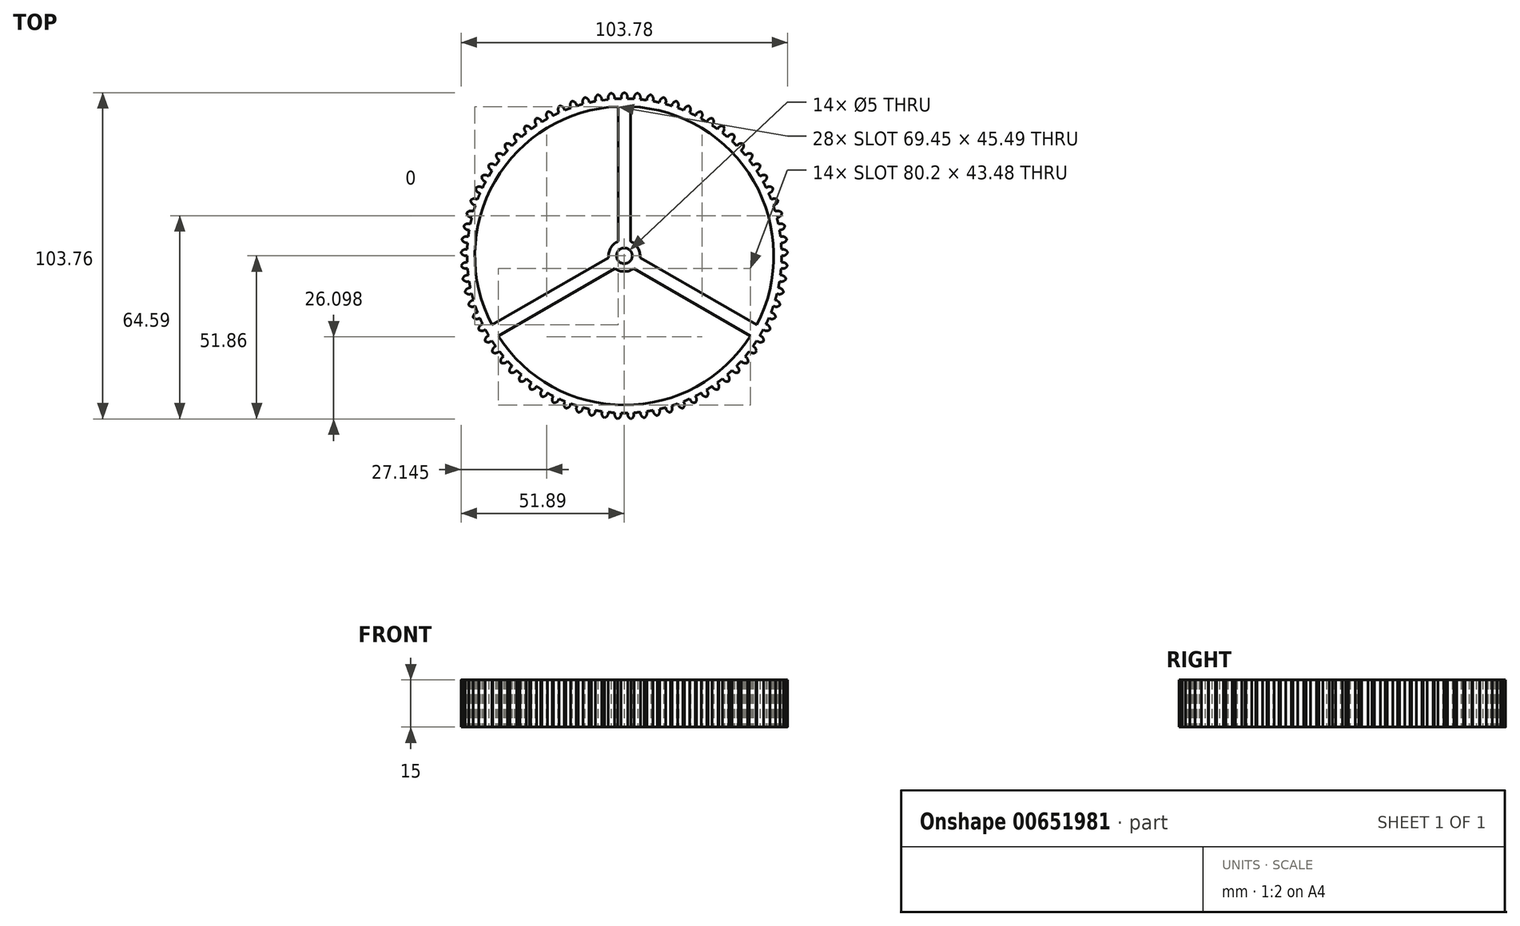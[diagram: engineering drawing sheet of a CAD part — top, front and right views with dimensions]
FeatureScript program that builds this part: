
annotation { "Feature Type Name" : "Feature", "Feature Type Description" : "" }
export const myFeature = defineFeature(function(context is Context, id is Id, definition is map)
    precondition{}
    {
        {
            var Q0;
            Q0=qCreatedBy(makeId("Top.planeOp"),FACE);
            var sketch = newSketch(context, id + "F0", { "sketchPlane" : qUnion([Q0])});
            skArc(sketch, "E0", {"start": v(-1, 49.99) * mm, "mid": v(-2.04, 49.96) * mm, "end": v(-3.08, 49.9) * mm});
            skLineSegment(sketch, "E1", {"start": v(-1, 49.99) * mm, "end": v(-1, 51.99) * mm});
            skLineSegment(sketch, "E2", {"start": v(-1, 51.99) * mm, "end": v(1, 51.99) * mm});
            skLineSegment(sketch, "E3", {"start": v(1, 51.99) * mm, "end": v(1, 49.99) * mm});
            skLineSegment(sketch, "E4.1.0", {"start": v(-5.23, 51.74) * mm, "end": v(-3.24, 51.9) * mm});
            skLineSegment(sketch, "E4.1.1", {"start": v(-3.24, 51.9) * mm, "end": v(-3.08, 49.9) * mm});
            skLineSegment(sketch, "E4.1.2", {"start": v(-5.07, 49.74) * mm, "end": v(-5.23, 51.74) * mm});
            skLineSegment(sketch, "E4.2.0", {"start": v(-9.43, 51.14) * mm, "end": v(-7.46, 51.46) * mm});
            skLineSegment(sketch, "E4.2.1", {"start": v(-7.46, 51.46) * mm, "end": v(-7.14, 49.49) * mm});
            skLineSegment(sketch, "E4.2.2", {"start": v(-9.1, 49.16) * mm, "end": v(-9.43, 51.14) * mm});
            skLineSegment(sketch, "E4.3.0", {"start": v(-13.57, 50.2) * mm, "end": v(-11.63, 50.68) * mm});
            skLineSegment(sketch, "E4.3.1", {"start": v(-11.63, 50.68) * mm, "end": v(-11.14, 48.74) * mm});
            skLineSegment(sketch, "E4.3.2", {"start": v(-13.09, 48.26) * mm, "end": v(-13.57, 50.2) * mm});
            skLineSegment(sketch, "E4.4.0", {"start": v(-17.62, 48.92) * mm, "end": v(-15.72, 49.57) * mm});
            skLineSegment(sketch, "E4.4.1", {"start": v(-15.72, 49.57) * mm, "end": v(-15.08, 47.67) * mm});
            skLineSegment(sketch, "E4.4.2", {"start": v(-16.98, 47.03) * mm, "end": v(-17.62, 48.92) * mm});
            skLineSegment(sketch, "E4.5.0", {"start": v(-21.55, 47.33) * mm, "end": v(-19.7, 48.12) * mm});
            skLineSegment(sketch, "E4.5.1", {"start": v(-19.7, 48.12) * mm, "end": v(-18.92, 46.28) * mm});
            skLineSegment(sketch, "E4.5.2", {"start": v(-20.75, 45.5) * mm, "end": v(-21.55, 47.33) * mm});
            skLineSegment(sketch, "E4.6.0", {"start": v(-25.33, 45.41) * mm, "end": v(-23.57, 46.35) * mm});
            skLineSegment(sketch, "E4.6.1", {"start": v(-23.57, 46.35) * mm, "end": v(-22.63, 44.59) * mm});
            skLineSegment(sketch, "E4.6.2", {"start": v(-24.4, 43.65) * mm, "end": v(-25.33, 45.41) * mm});
            skLineSegment(sketch, "E4.7.0", {"start": v(-28.95, 43.2) * mm, "end": v(-27.27, 44.28) * mm});
            skLineSegment(sketch, "E4.7.1", {"start": v(-27.27, 44.28) * mm, "end": v(-26.18, 42.6) * mm});
            skLineSegment(sketch, "E4.7.2", {"start": v(-27.87, 41.51) * mm, "end": v(-28.95, 43.2) * mm});
            skLineSegment(sketch, "E4.8.0", {"start": v(-32.37, 40.7) * mm, "end": v(-30.78, 41.9) * mm});
            skLineSegment(sketch, "E4.8.1", {"start": v(-30.78, 41.9) * mm, "end": v(-29.57, 40.32) * mm});
            skLineSegment(sketch, "E4.8.2", {"start": v(-31.16, 39.1) * mm, "end": v(-32.37, 40.7) * mm});
            skLineSegment(sketch, "E4.9.0", {"start": v(-35.58, 37.92) * mm, "end": v(-34.1, 39.26) * mm});
            skLineSegment(sketch, "E4.9.1", {"start": v(-34.1, 39.26) * mm, "end": v(-32.76, 37.78) * mm});
            skLineSegment(sketch, "E4.9.2", {"start": v(-34.24, 36.43) * mm, "end": v(-35.58, 37.92) * mm});
            skLineSegment(sketch, "E4.10.0", {"start": v(-38.55, 34.9) * mm, "end": v(-37.18, 36.35) * mm});
            skLineSegment(sketch, "E4.10.1", {"start": v(-37.18, 36.35) * mm, "end": v(-35.73, 34.98) * mm});
            skLineSegment(sketch, "E4.10.2", {"start": v(-37.1, 33.52) * mm, "end": v(-38.55, 34.9) * mm});
            skLineSegment(sketch, "E4.11.0", {"start": v(-41.27, 31.63) * mm, "end": v(-40.02, 33.2) * mm});
            skLineSegment(sketch, "E4.11.1", {"start": v(-40.02, 33.2) * mm, "end": v(-38.46, 31.95) * mm});
            skLineSegment(sketch, "E4.11.2", {"start": v(-39.7, 30.39) * mm, "end": v(-41.27, 31.63) * mm});
            skLineSegment(sketch, "E4.12.0", {"start": v(-43.71, 28.17) * mm, "end": v(-42.6, 29.83) * mm});
            skLineSegment(sketch, "E4.12.1", {"start": v(-42.6, 29.83) * mm, "end": v(-40.93, 28.7) * mm});
            skLineSegment(sketch, "E4.12.2", {"start": v(-42.05, 27.05) * mm, "end": v(-43.71, 28.17) * mm});
            skLineSegment(sketch, "E4.13.0", {"start": v(-45.86, 24.5) * mm, "end": v(-44.88, 26.25) * mm});
            skLineSegment(sketch, "E4.13.1", {"start": v(-44.88, 26.25) * mm, "end": v(-43.14, 25.28) * mm});
            skLineSegment(sketch, "E4.13.2", {"start": v(-44.11, 23.53) * mm, "end": v(-45.86, 24.5) * mm});
            skLineSegment(sketch, "E4.14.0", {"start": v(-47.7, 20.69) * mm, "end": v(-46.87, 22.5) * mm});
            skLineSegment(sketch, "E4.14.1", {"start": v(-46.87, 22.5) * mm, "end": v(-45.06, 21.68) * mm});
            skLineSegment(sketch, "E4.14.2", {"start": v(-45.89, 19.86) * mm, "end": v(-47.7, 20.69) * mm});
            skLineSegment(sketch, "E4.15.0", {"start": v(-49.23, 16.73) * mm, "end": v(-48.55, 18.61) * mm});
            skLineSegment(sketch, "E4.15.1", {"start": v(-48.55, 18.61) * mm, "end": v(-46.67, 17.93) * mm});
            skLineSegment(sketch, "E4.15.2", {"start": v(-47.35, 16.05) * mm, "end": v(-49.23, 16.73) * mm});
            skLineSegment(sketch, "E4.16.0", {"start": v(-50.43, 12.66) * mm, "end": v(-49.9, 14.6) * mm});
            skLineSegment(sketch, "E4.16.1", {"start": v(-49.9, 14.6) * mm, "end": v(-47.98, 14.07) * mm});
            skLineSegment(sketch, "E4.16.2", {"start": v(-48.5, 12.14) * mm, "end": v(-50.43, 12.66) * mm});
            skLineSegment(sketch, "E4.17.0", {"start": v(-51.3, 8.51) * mm, "end": v(-50.93, 10.48) * mm});
            skLineSegment(sketch, "E4.17.1", {"start": v(-50.93, 10.48) * mm, "end": v(-48.97, 10.11) * mm});
            skLineSegment(sketch, "E4.17.2", {"start": v(-49.33, 8.15) * mm, "end": v(-51.3, 8.51) * mm});
            skLineSegment(sketch, "E4.18.0", {"start": v(-51.82, 4.3) * mm, "end": v(-51.62, 6.3) * mm});
            skLineSegment(sketch, "E4.18.1", {"start": v(-51.62, 6.3) * mm, "end": v(-49.63, 6.09) * mm});
            skLineSegment(sketch, "E4.18.2", {"start": v(-49.83, 4.1) * mm, "end": v(-51.82, 4.3) * mm});
            skLineSegment(sketch, "E4.19.0", {"start": v(-52, 0.06) * mm, "end": v(-51.96, 2.06) * mm});
            skLineSegment(sketch, "E4.19.1", {"start": v(-51.96, 2.06) * mm, "end": v(-49.96, 2.02) * mm});
            skLineSegment(sketch, "E4.19.2", {"start": v(-50, 0.02) * mm, "end": v(-52, 0.06) * mm});
            skLineSegment(sketch, "E4.20.0", {"start": v(-51.83, -4.18) * mm, "end": v(-51.95, -2.18) * mm});
            skLineSegment(sketch, "E4.20.1", {"start": v(-51.95, -2.18) * mm, "end": v(-49.96, -2.06) * mm});
            skLineSegment(sketch, "E4.20.2", {"start": v(-49.83, -4.05) * mm, "end": v(-51.83, -4.18) * mm});
            skLineSegment(sketch, "E4.21.0", {"start": v(-51.32, -8.39) * mm, "end": v(-51.6, -6.4) * mm});
            skLineSegment(sketch, "E4.21.1", {"start": v(-51.6, -6.4) * mm, "end": v(-49.62, -6.12) * mm});
            skLineSegment(sketch, "E4.21.2", {"start": v(-49.34, -8.1) * mm, "end": v(-51.32, -8.39) * mm});
            skLineSegment(sketch, "E4.22.0", {"start": v(-50.46, -12.54) * mm, "end": v(-50.9, -10.6) * mm});
            skLineSegment(sketch, "E4.22.1", {"start": v(-50.9, -10.6) * mm, "end": v(-48.96, -10.15) * mm});
            skLineSegment(sketch, "E4.22.2", {"start": v(-48.51, -12.1) * mm, "end": v(-50.46, -12.54) * mm});
            skLineSegment(sketch, "E4.23.0", {"start": v(-49.27, -16.61) * mm, "end": v(-49.87, -14.7) * mm});
            skLineSegment(sketch, "E4.23.1", {"start": v(-49.87, -14.7) * mm, "end": v(-47.97, -14.1) * mm});
            skLineSegment(sketch, "E4.23.2", {"start": v(-47.36, -16.01) * mm, "end": v(-49.27, -16.61) * mm});
            skLineSegment(sketch, "E4.24.0", {"start": v(-47.75, -20.57) * mm, "end": v(-48.5, -18.72) * mm});
            skLineSegment(sketch, "E4.24.1", {"start": v(-48.5, -18.72) * mm, "end": v(-46.66, -17.97) * mm});
            skLineSegment(sketch, "E4.24.2", {"start": v(-45.9, -19.82) * mm, "end": v(-47.75, -20.57) * mm});
            skLineSegment(sketch, "E4.25.0", {"start": v(-45.92, -24.4) * mm, "end": v(-46.82, -22.61) * mm});
            skLineSegment(sketch, "E4.25.1", {"start": v(-46.82, -22.61) * mm, "end": v(-45.04, -21.7) * mm});
            skLineSegment(sketch, "E4.25.2", {"start": v(-44.13, -23.5) * mm, "end": v(-45.92, -24.4) * mm});
            skLineSegment(sketch, "E4.26.0", {"start": v(-43.78, -28.06) * mm, "end": v(-44.82, -26.35) * mm});
            skLineSegment(sketch, "E4.26.1", {"start": v(-44.82, -26.35) * mm, "end": v(-43.12, -25.3) * mm});
            skLineSegment(sketch, "E4.26.2", {"start": v(-42.07, -27.01) * mm, "end": v(-43.78, -28.06) * mm});
            skLineSegment(sketch, "E4.27.0", {"start": v(-41.34, -31.53) * mm, "end": v(-42.53, -29.92) * mm});
            skLineSegment(sketch, "E4.27.1", {"start": v(-42.53, -29.92) * mm, "end": v(-40.91, -28.74) * mm});
            skLineSegment(sketch, "E4.27.2", {"start": v(-39.73, -30.35) * mm, "end": v(-41.34, -31.53) * mm});
            skLineSegment(sketch, "E4.28.0", {"start": v(-38.64, -34.8) * mm, "end": v(-39.94, -33.29) * mm});
            skLineSegment(sketch, "E4.28.1", {"start": v(-39.94, -33.29) * mm, "end": v(-38.43, -31.98) * mm});
            skLineSegment(sketch, "E4.28.2", {"start": v(-37.12, -33.49) * mm, "end": v(-38.64, -34.8) * mm});
            skLineSegment(sketch, "E4.29.0", {"start": v(-35.67, -37.83) * mm, "end": v(-37.1, -36.43) * mm});
            skLineSegment(sketch, "E4.29.1", {"start": v(-37.1, -36.43) * mm, "end": v(-35.7, -35) * mm});
            skLineSegment(sketch, "E4.29.2", {"start": v(-34.27, -36.4) * mm, "end": v(-35.67, -37.83) * mm});
            skLineSegment(sketch, "E4.30.0", {"start": v(-32.47, -40.61) * mm, "end": v(-34, -39.33) * mm});
            skLineSegment(sketch, "E4.30.1", {"start": v(-34, -39.33) * mm, "end": v(-32.73, -37.8) * mm});
            skLineSegment(sketch, "E4.30.2", {"start": v(-31.19, -39.08) * mm, "end": v(-32.47, -40.61) * mm});
            skLineSegment(sketch, "E4.31.0", {"start": v(-29.05, -43.12) * mm, "end": v(-30.69, -41.98) * mm});
            skLineSegment(sketch, "E4.31.1", {"start": v(-30.69, -41.98) * mm, "end": v(-29.54, -40.34) * mm});
            skLineSegment(sketch, "E4.31.2", {"start": v(-27.9, -41.49) * mm, "end": v(-29.05, -43.12) * mm});
            skLineSegment(sketch, "E4.32.0", {"start": v(-25.44, -45.35) * mm, "end": v(-27.16, -44.34) * mm});
            skLineSegment(sketch, "E4.32.1", {"start": v(-27.16, -44.34) * mm, "end": v(-26.15, -42.61) * mm});
            skLineSegment(sketch, "E4.32.2", {"start": v(-24.43, -43.62) * mm, "end": v(-25.44, -45.35) * mm});
            skLineSegment(sketch, "E4.33.0", {"start": v(-21.66, -47.27) * mm, "end": v(-23.46, -46.4) * mm});
            skLineSegment(sketch, "E4.33.1", {"start": v(-23.46, -46.4) * mm, "end": v(-22.6, -44.6) * mm});
            skLineSegment(sketch, "E4.33.2", {"start": v(-20.79, -45.47) * mm, "end": v(-21.66, -47.27) * mm});
            skLineSegment(sketch, "E4.34.0", {"start": v(-17.73, -48.88) * mm, "end": v(-19.6, -48.16) * mm});
            skLineSegment(sketch, "E4.34.1", {"start": v(-19.6, -48.16) * mm, "end": v(-18.88, -46.3) * mm});
            skLineSegment(sketch, "E4.34.2", {"start": v(-17.01, -47.01) * mm, "end": v(-17.73, -48.88) * mm});
            skLineSegment(sketch, "E4.35.0", {"start": v(-13.69, -50.16) * mm, "end": v(-15.6, -49.6) * mm});
            skLineSegment(sketch, "E4.35.1", {"start": v(-15.6, -49.6) * mm, "end": v(-15.04, -47.68) * mm});
            skLineSegment(sketch, "E4.35.2", {"start": v(-13.12, -48.24) * mm, "end": v(-13.69, -50.16) * mm});
            skLineSegment(sketch, "E4.36.0", {"start": v(-9.55, -51.11) * mm, "end": v(-11.51, -50.7) * mm});
            skLineSegment(sketch, "E4.36.1", {"start": v(-11.51, -50.7) * mm, "end": v(-11.1, -48.75) * mm});
            skLineSegment(sketch, "E4.36.2", {"start": v(-9.15, -49.15) * mm, "end": v(-9.55, -51.11) * mm});
            skLineSegment(sketch, "E4.37.0", {"start": v(-5.36, -51.72) * mm, "end": v(-7.34, -51.47) * mm});
            skLineSegment(sketch, "E4.37.1", {"start": v(-7.34, -51.47) * mm, "end": v(-7.1, -49.49) * mm});
            skLineSegment(sketch, "E4.37.2", {"start": v(-5.11, -49.73) * mm, "end": v(-5.36, -51.72) * mm});
            skLineSegment(sketch, "E4.38.0", {"start": v(-1.12, -51.98) * mm, "end": v(-3.12, -51.9) * mm});
            skLineSegment(sketch, "E4.38.1", {"start": v(-3.12, -51.9) * mm, "end": v(-3.04, -49.9) * mm});
            skLineSegment(sketch, "E4.38.2", {"start": v(-1.04, -49.98) * mm, "end": v(-1.12, -51.98) * mm});
            skLineSegment(sketch, "E4.39.0", {"start": v(3.12, -51.9) * mm, "end": v(1.12, -51.98) * mm});
            skLineSegment(sketch, "E4.39.1", {"start": v(1.12, -51.98) * mm, "end": v(1.04, -49.98) * mm});
            skLineSegment(sketch, "E4.39.2", {"start": v(3.04, -49.9) * mm, "end": v(3.12, -51.9) * mm});
            skLineSegment(sketch, "E4.40.0", {"start": v(7.34, -51.47) * mm, "end": v(5.35, -51.72) * mm});
            skLineSegment(sketch, "E4.40.1", {"start": v(5.35, -51.72) * mm, "end": v(5.11, -49.73) * mm});
            skLineSegment(sketch, "E4.40.2", {"start": v(7.1, -49.49) * mm, "end": v(7.34, -51.47) * mm});
            skLineSegment(sketch, "E4.41.0", {"start": v(11.51, -50.7) * mm, "end": v(9.55, -51.11) * mm});
            skLineSegment(sketch, "E4.41.1", {"start": v(9.55, -51.11) * mm, "end": v(9.15, -49.15) * mm});
            skLineSegment(sketch, "E4.41.2", {"start": v(11.1, -48.75) * mm, "end": v(11.51, -50.7) * mm});
            skLineSegment(sketch, "E4.42.0", {"start": v(15.6, -49.6) * mm, "end": v(13.69, -50.16) * mm});
            skLineSegment(sketch, "E4.42.1", {"start": v(13.69, -50.16) * mm, "end": v(13.12, -48.24) * mm});
            skLineSegment(sketch, "E4.42.2", {"start": v(15.04, -47.68) * mm, "end": v(15.6, -49.6) * mm});
            skLineSegment(sketch, "E4.43.0", {"start": v(19.6, -48.16) * mm, "end": v(17.73, -48.88) * mm});
            skLineSegment(sketch, "E4.43.1", {"start": v(17.73, -48.88) * mm, "end": v(17.01, -47.01) * mm});
            skLineSegment(sketch, "E4.43.2", {"start": v(18.88, -46.3) * mm, "end": v(19.6, -48.16) * mm});
            skLineSegment(sketch, "E4.44.0", {"start": v(23.46, -46.4) * mm, "end": v(21.66, -47.27) * mm});
            skLineSegment(sketch, "E4.44.1", {"start": v(21.66, -47.27) * mm, "end": v(20.79, -45.47) * mm});
            skLineSegment(sketch, "E4.44.2", {"start": v(22.59, -44.6) * mm, "end": v(23.46, -46.4) * mm});
            skLineSegment(sketch, "E4.45.0", {"start": v(27.16, -44.34) * mm, "end": v(25.44, -45.35) * mm});
            skLineSegment(sketch, "E4.45.1", {"start": v(25.44, -45.35) * mm, "end": v(24.42, -43.62) * mm});
            skLineSegment(sketch, "E4.45.2", {"start": v(26.15, -42.61) * mm, "end": v(27.16, -44.34) * mm});
            skLineSegment(sketch, "E4.46.0", {"start": v(30.69, -41.98) * mm, "end": v(29.05, -43.12) * mm});
            skLineSegment(sketch, "E4.46.1", {"start": v(29.05, -43.12) * mm, "end": v(27.9, -41.49) * mm});
            skLineSegment(sketch, "E4.46.2", {"start": v(29.54, -40.34) * mm, "end": v(30.69, -41.98) * mm});
            skLineSegment(sketch, "E4.47.0", {"start": v(34, -39.33) * mm, "end": v(32.47, -40.61) * mm});
            skLineSegment(sketch, "E4.47.1", {"start": v(32.47, -40.61) * mm, "end": v(31.19, -39.08) * mm});
            skLineSegment(sketch, "E4.47.2", {"start": v(32.73, -37.8) * mm, "end": v(34, -39.33) * mm});
            skLineSegment(sketch, "E4.48.0", {"start": v(37.1, -36.43) * mm, "end": v(35.67, -37.83) * mm});
            skLineSegment(sketch, "E4.48.1", {"start": v(35.67, -37.83) * mm, "end": v(34.27, -36.4) * mm});
            skLineSegment(sketch, "E4.48.2", {"start": v(35.7, -35) * mm, "end": v(37.1, -36.43) * mm});
            skLineSegment(sketch, "E4.49.0", {"start": v(39.94, -33.29) * mm, "end": v(38.63, -34.8) * mm});
            skLineSegment(sketch, "E4.49.1", {"start": v(38.63, -34.8) * mm, "end": v(37.12, -33.49) * mm});
            skLineSegment(sketch, "E4.49.2", {"start": v(38.43, -31.98) * mm, "end": v(39.94, -33.29) * mm});
            skLineSegment(sketch, "E4.50.0", {"start": v(42.52, -29.92) * mm, "end": v(41.34, -31.53) * mm});
            skLineSegment(sketch, "E4.50.1", {"start": v(41.34, -31.53) * mm, "end": v(39.73, -30.35) * mm});
            skLineSegment(sketch, "E4.50.2", {"start": v(40.91, -28.74) * mm, "end": v(42.52, -29.92) * mm});
            skLineSegment(sketch, "E4.51.0", {"start": v(44.82, -26.35) * mm, "end": v(43.78, -28.06) * mm});
            skLineSegment(sketch, "E4.51.1", {"start": v(43.78, -28.06) * mm, "end": v(42.07, -27.01) * mm});
            skLineSegment(sketch, "E4.51.2", {"start": v(43.12, -25.3) * mm, "end": v(44.82, -26.35) * mm});
            skLineSegment(sketch, "E4.52.0", {"start": v(46.82, -22.61) * mm, "end": v(45.92, -24.4) * mm});
            skLineSegment(sketch, "E4.52.1", {"start": v(45.92, -24.4) * mm, "end": v(44.13, -23.5) * mm});
            skLineSegment(sketch, "E4.52.2", {"start": v(45.04, -21.7) * mm, "end": v(46.82, -22.61) * mm});
            skLineSegment(sketch, "E4.53.0", {"start": v(48.5, -18.72) * mm, "end": v(47.75, -20.57) * mm});
            skLineSegment(sketch, "E4.53.1", {"start": v(47.75, -20.57) * mm, "end": v(45.9, -19.82) * mm});
            skLineSegment(sketch, "E4.53.2", {"start": v(46.66, -17.97) * mm, "end": v(48.5, -18.72) * mm});
            skLineSegment(sketch, "E4.54.0", {"start": v(49.87, -14.7) * mm, "end": v(49.27, -16.61) * mm});
            skLineSegment(sketch, "E4.54.1", {"start": v(49.27, -16.61) * mm, "end": v(47.36, -16.01) * mm});
            skLineSegment(sketch, "E4.54.2", {"start": v(47.97, -14.1) * mm, "end": v(49.87, -14.7) * mm});
            skLineSegment(sketch, "E4.55.0", {"start": v(50.9, -10.6) * mm, "end": v(50.46, -12.54) * mm});
            skLineSegment(sketch, "E4.55.1", {"start": v(50.46, -12.54) * mm, "end": v(48.51, -12.1) * mm});
            skLineSegment(sketch, "E4.55.2", {"start": v(48.96, -10.15) * mm, "end": v(50.9, -10.6) * mm});
            skLineSegment(sketch, "E4.56.0", {"start": v(51.6, -6.4) * mm, "end": v(51.32, -8.39) * mm});
            skLineSegment(sketch, "E4.56.1", {"start": v(51.32, -8.39) * mm, "end": v(49.34, -8.1) * mm});
            skLineSegment(sketch, "E4.56.2", {"start": v(49.62, -6.12) * mm, "end": v(51.6, -6.4) * mm});
            skLineSegment(sketch, "E4.57.0", {"start": v(51.95, -2.18) * mm, "end": v(51.83, -4.18) * mm});
            skLineSegment(sketch, "E4.57.1", {"start": v(51.83, -4.18) * mm, "end": v(49.83, -4.05) * mm});
            skLineSegment(sketch, "E4.57.2", {"start": v(49.96, -2.06) * mm, "end": v(51.95, -2.18) * mm});
            skLineSegment(sketch, "E4.58.0", {"start": v(51.96, 2.06) * mm, "end": v(52, 0.06) * mm});
            skLineSegment(sketch, "E4.58.1", {"start": v(52, 0.06) * mm, "end": v(50, 0.02) * mm});
            skLineSegment(sketch, "E4.58.2", {"start": v(49.96, 2.02) * mm, "end": v(51.96, 2.06) * mm});
            skLineSegment(sketch, "E4.59.0", {"start": v(51.62, 6.3) * mm, "end": v(51.82, 4.3) * mm});
            skLineSegment(sketch, "E4.59.1", {"start": v(51.82, 4.3) * mm, "end": v(49.83, 4.1) * mm});
            skLineSegment(sketch, "E4.59.2", {"start": v(49.63, 6.09) * mm, "end": v(51.62, 6.3) * mm});
            skLineSegment(sketch, "E4.60.0", {"start": v(50.93, 10.48) * mm, "end": v(51.3, 8.51) * mm});
            skLineSegment(sketch, "E4.60.1", {"start": v(51.3, 8.51) * mm, "end": v(49.33, 8.15) * mm});
            skLineSegment(sketch, "E4.60.2", {"start": v(48.97, 10.11) * mm, "end": v(50.93, 10.48) * mm});
            skLineSegment(sketch, "E4.61.0", {"start": v(49.9, 14.6) * mm, "end": v(50.43, 12.66) * mm});
            skLineSegment(sketch, "E4.61.1", {"start": v(50.43, 12.66) * mm, "end": v(48.5, 12.14) * mm});
            skLineSegment(sketch, "E4.61.2", {"start": v(47.98, 14.07) * mm, "end": v(49.9, 14.6) * mm});
            skLineSegment(sketch, "E4.62.0", {"start": v(48.55, 18.61) * mm, "end": v(49.23, 16.73) * mm});
            skLineSegment(sketch, "E4.62.1", {"start": v(49.23, 16.73) * mm, "end": v(47.35, 16.05) * mm});
            skLineSegment(sketch, "E4.62.2", {"start": v(46.67, 17.93) * mm, "end": v(48.55, 18.61) * mm});
            skLineSegment(sketch, "E4.63.0", {"start": v(46.87, 22.5) * mm, "end": v(47.7, 20.69) * mm});
            skLineSegment(sketch, "E4.63.1", {"start": v(47.7, 20.69) * mm, "end": v(45.89, 19.86) * mm});
            skLineSegment(sketch, "E4.63.2", {"start": v(45.06, 21.68) * mm, "end": v(46.87, 22.5) * mm});
            skLineSegment(sketch, "E4.64.0", {"start": v(44.88, 26.25) * mm, "end": v(45.86, 24.5) * mm});
            skLineSegment(sketch, "E4.64.1", {"start": v(45.86, 24.5) * mm, "end": v(44.11, 23.53) * mm});
            skLineSegment(sketch, "E4.64.2", {"start": v(43.14, 25.28) * mm, "end": v(44.88, 26.25) * mm});
            skLineSegment(sketch, "E4.65.0", {"start": v(42.6, 29.83) * mm, "end": v(43.71, 28.17) * mm});
            skLineSegment(sketch, "E4.65.1", {"start": v(43.71, 28.17) * mm, "end": v(42.05, 27.05) * mm});
            skLineSegment(sketch, "E4.65.2", {"start": v(40.93, 28.7) * mm, "end": v(42.6, 29.83) * mm});
            skLineSegment(sketch, "E4.66.0", {"start": v(40.02, 33.2) * mm, "end": v(41.27, 31.63) * mm});
            skLineSegment(sketch, "E4.66.1", {"start": v(41.27, 31.63) * mm, "end": v(39.7, 30.39) * mm});
            skLineSegment(sketch, "E4.66.2", {"start": v(38.46, 31.95) * mm, "end": v(40.02, 33.2) * mm});
            skLineSegment(sketch, "E4.67.0", {"start": v(37.18, 36.35) * mm, "end": v(38.55, 34.9) * mm});
            skLineSegment(sketch, "E4.67.1", {"start": v(38.55, 34.9) * mm, "end": v(37.1, 33.52) * mm});
            skLineSegment(sketch, "E4.67.2", {"start": v(35.73, 34.98) * mm, "end": v(37.18, 36.35) * mm});
            skLineSegment(sketch, "E4.68.0", {"start": v(34.1, 39.26) * mm, "end": v(35.58, 37.92) * mm});
            skLineSegment(sketch, "E4.68.1", {"start": v(35.58, 37.92) * mm, "end": v(34.24, 36.43) * mm});
            skLineSegment(sketch, "E4.68.2", {"start": v(32.76, 37.77) * mm, "end": v(34.1, 39.26) * mm});
            skLineSegment(sketch, "E4.69.0", {"start": v(30.78, 41.9) * mm, "end": v(32.37, 40.7) * mm});
            skLineSegment(sketch, "E4.69.1", {"start": v(32.37, 40.7) * mm, "end": v(31.16, 39.1) * mm});
            skLineSegment(sketch, "E4.69.2", {"start": v(29.57, 40.32) * mm, "end": v(30.78, 41.9) * mm});
            skLineSegment(sketch, "E4.70.0", {"start": v(27.27, 44.28) * mm, "end": v(28.95, 43.2) * mm});
            skLineSegment(sketch, "E4.70.1", {"start": v(28.95, 43.2) * mm, "end": v(27.87, 41.51) * mm});
            skLineSegment(sketch, "E4.70.2", {"start": v(26.18, 42.6) * mm, "end": v(27.27, 44.28) * mm});
            skLineSegment(sketch, "E4.71.0", {"start": v(23.57, 46.35) * mm, "end": v(25.33, 45.41) * mm});
            skLineSegment(sketch, "E4.71.1", {"start": v(25.33, 45.41) * mm, "end": v(24.4, 43.65) * mm});
            skLineSegment(sketch, "E4.71.2", {"start": v(22.63, 44.59) * mm, "end": v(23.57, 46.35) * mm});
            skLineSegment(sketch, "E4.72.0", {"start": v(19.7, 48.12) * mm, "end": v(21.55, 47.33) * mm});
            skLineSegment(sketch, "E4.72.1", {"start": v(21.55, 47.33) * mm, "end": v(20.75, 45.5) * mm});
            skLineSegment(sketch, "E4.72.2", {"start": v(18.92, 46.28) * mm, "end": v(19.7, 48.12) * mm});
            skLineSegment(sketch, "E4.73.0", {"start": v(15.72, 49.57) * mm, "end": v(17.62, 48.92) * mm});
            skLineSegment(sketch, "E4.73.1", {"start": v(17.62, 48.92) * mm, "end": v(16.98, 47.03) * mm});
            skLineSegment(sketch, "E4.73.2", {"start": v(15.08, 47.67) * mm, "end": v(15.72, 49.57) * mm});
            skLineSegment(sketch, "E4.74.0", {"start": v(11.63, 50.68) * mm, "end": v(13.57, 50.2) * mm});
            skLineSegment(sketch, "E4.74.1", {"start": v(13.57, 50.2) * mm, "end": v(13.09, 48.26) * mm});
            skLineSegment(sketch, "E4.74.2", {"start": v(11.14, 48.74) * mm, "end": v(11.63, 50.68) * mm});
            skLineSegment(sketch, "E4.75.0", {"start": v(7.46, 51.46) * mm, "end": v(9.43, 51.14) * mm});
            skLineSegment(sketch, "E4.75.1", {"start": v(9.43, 51.14) * mm, "end": v(9.1, 49.16) * mm});
            skLineSegment(sketch, "E4.75.2", {"start": v(7.14, 49.49) * mm, "end": v(7.46, 51.46) * mm});
            skLineSegment(sketch, "E4.76.0", {"start": v(3.24, 51.9) * mm, "end": v(5.23, 51.74) * mm});
            skLineSegment(sketch, "E4.76.1", {"start": v(5.23, 51.74) * mm, "end": v(5.07, 49.74) * mm});
            skLineSegment(sketch, "E4.76.2", {"start": v(3.08, 49.9) * mm, "end": v(3.24, 51.9) * mm});
            skArc(sketch, "E5.trimOffspring", {"start": v(-9.1, 49.16) * mm, "mid": v(-10.13, 48.96) * mm, "end": v(-11.14, 48.74) * mm});
            skArc(sketch, "E6.trimOffspring", {"start": v(-13.09, 48.26) * mm, "mid": v(-14.09, 47.97) * mm, "end": v(-15.08, 47.67) * mm});
            skArc(sketch, "E7.trimOffspring", {"start": v(-16.98, 47.03) * mm, "mid": v(-17.95, 46.67) * mm, "end": v(-18.92, 46.28) * mm});
            skArc(sketch, "E8.trimOffspring", {"start": v(-20.75, 45.5) * mm, "mid": v(-21.7, 45.05) * mm, "end": v(-22.63, 44.59) * mm});
            skArc(sketch, "E9.trimOffspring", {"start": v(-24.4, 43.65) * mm, "mid": v(-25.3, 43.13) * mm, "end": v(-26.18, 42.6) * mm});
            skArc(sketch, "E10.trimOffspring", {"start": v(-27.87, 41.51) * mm, "mid": v(-28.72, 40.93) * mm, "end": v(-29.57, 40.32) * mm});
            skArc(sketch, "E11.trimOffspring", {"start": v(-31.16, 39.1) * mm, "mid": v(-31.96, 38.45) * mm, "end": v(-32.76, 37.78) * mm});
            skArc(sketch, "E12.trimOffspring", {"start": v(-34.24, 36.43) * mm, "mid": v(-35, 35.71) * mm, "end": v(-35.73, 34.98) * mm});
            skArc(sketch, "E13.trimOffspring", {"start": v(-37.1, 33.52) * mm, "mid": v(-37.79, 32.74) * mm, "end": v(-38.46, 31.95) * mm});
            skArc(sketch, "E14.trimOffspring", {"start": v(-39.7, 30.39) * mm, "mid": v(-40.33, 29.55) * mm, "end": v(-40.93, 28.7) * mm});
            skArc(sketch, "E15.trimOffspring", {"start": v(-44.11, 23.53) * mm, "mid": v(-44.6, 22.6) * mm, "end": v(-45.06, 21.68) * mm});
            skArc(sketch, "E16.trimOffspring", {"start": v(-45.89, 19.86) * mm, "mid": v(-46.29, 18.9) * mm, "end": v(-46.67, 17.93) * mm});
            skArc(sketch, "E17.trimOffspring", {"start": v(-47.35, 16.05) * mm, "mid": v(-47.68, 15.06) * mm, "end": v(-47.98, 14.07) * mm});
            skArc(sketch, "E18.trimOffspring", {"start": v(-48.5, 12.14) * mm, "mid": v(-48.74, 11.13) * mm, "end": v(-48.97, 10.11) * mm});
            skArc(sketch, "E19.trimOffspring", {"start": v(-49.33, 8.15) * mm, "mid": v(-49.49, 7.12) * mm, "end": v(-49.63, 6.09) * mm});
            skArc(sketch, "E20.trimOffspring", {"start": v(-49.83, 4.1) * mm, "mid": v(-49.9, 3.06) * mm, "end": v(-49.96, 2.02) * mm});
            skArc(sketch, "E21.trimOffspring", {"start": v(-50, 0.02) * mm, "mid": v(-49.99, -1.02) * mm, "end": v(-49.96, -2.06) * mm});
            skArc(sketch, "E22.trimOffspring", {"start": v(-49.83, -4.05) * mm, "mid": v(-49.74, -5.09) * mm, "end": v(-49.62, -6.12) * mm});
            skArc(sketch, "E23.trimOffspring", {"start": v(-49.34, -8.1) * mm, "mid": v(-49.16, -9.13) * mm, "end": v(-48.96, -10.15) * mm});
            skLineSegment(sketch, "E24", {"start": v(-43.14, 25.28) * mm, "end": v(-42.05, 27.05) * mm});
            skArc(sketch, "E25.trimOffspring", {"start": v(3.08, 49.9) * mm, "mid": v(2.04, 49.96) * mm, "end": v(1, 49.99) * mm});
            skArc(sketch, "E26.trimOffspring", {"start": v(7.14, 49.49) * mm, "mid": v(6.1, 49.63) * mm, "end": v(5.07, 49.74) * mm});
            skArc(sketch, "E27.trimOffspring", {"start": v(11.14, 48.74) * mm, "mid": v(10.13, 48.96) * mm, "end": v(9.1, 49.16) * mm});
            skArc(sketch, "E28.trimOffspring", {"start": v(15.08, 47.67) * mm, "mid": v(14.09, 47.97) * mm, "end": v(13.09, 48.26) * mm});
            skArc(sketch, "E29.trimOffspring", {"start": v(18.92, 46.28) * mm, "mid": v(17.95, 46.67) * mm, "end": v(16.98, 47.03) * mm});
            skArc(sketch, "E30.trimOffspring", {"start": v(22.63, 44.59) * mm, "mid": v(21.7, 45.05) * mm, "end": v(20.75, 45.5) * mm});
            skArc(sketch, "E31.trimOffspring", {"start": v(26.18, 42.6) * mm, "mid": v(25.3, 43.13) * mm, "end": v(24.4, 43.65) * mm});
            skArc(sketch, "E32.trimOffspring", {"start": v(29.57, 40.32) * mm, "mid": v(28.72, 40.93) * mm, "end": v(27.87, 41.51) * mm});
            skArc(sketch, "E33.trimOffspring", {"start": v(32.76, 37.77) * mm, "mid": v(31.96, 38.45) * mm, "end": v(31.16, 39.1) * mm});
            skArc(sketch, "E34.trimOffspring", {"start": v(35.73, 34.98) * mm, "mid": v(35, 35.71) * mm, "end": v(34.24, 36.43) * mm});
            skArc(sketch, "E35.trimOffspring", {"start": v(38.46, 31.95) * mm, "mid": v(37.79, 32.74) * mm, "end": v(37.1, 33.52) * mm});
            skLineSegment(sketch, "E36", {"start": v(-7.14, 49.49) * mm, "end": v(-5.07, 49.74) * mm});
            skArc(sketch, "E37.trimOffspring", {"start": v(40.93, 28.7) * mm, "mid": v(40.33, 29.55) * mm, "end": v(39.7, 30.39) * mm});
            skArc(sketch, "E38.trimOffspring", {"start": v(43.14, 25.28) * mm, "mid": v(42.6, 26.17) * mm, "end": v(42.05, 27.05) * mm});
            skArc(sketch, "E39.trimOffspring", {"start": v(45.06, 21.68) * mm, "mid": v(44.6, 22.6) * mm, "end": v(44.11, 23.53) * mm});
            skArc(sketch, "E40.trimOffspring", {"start": v(46.67, 17.93) * mm, "mid": v(46.29, 18.9) * mm, "end": v(45.89, 19.86) * mm});
            skArc(sketch, "E41.trimOffspring", {"start": v(47.98, 14.07) * mm, "mid": v(47.68, 15.06) * mm, "end": v(47.35, 16.05) * mm});
            skArc(sketch, "E42.trimOffspring", {"start": v(48.97, 10.11) * mm, "mid": v(48.74, 11.13) * mm, "end": v(48.5, 12.14) * mm});
            skArc(sketch, "E43.trimOffspring", {"start": v(49.63, 6.09) * mm, "mid": v(49.49, 7.12) * mm, "end": v(49.33, 8.15) * mm});
            skArc(sketch, "E44.trimOffspring", {"start": v(49.96, 2.02) * mm, "mid": v(49.9, 3.06) * mm, "end": v(49.83, 4.1) * mm});
            skArc(sketch, "E45.trimOffspring", {"start": v(49.96, -2.06) * mm, "mid": v(49.99, -1.02) * mm, "end": v(50, 0.02) * mm});
            skArc(sketch, "E46.trimOffspring", {"start": v(49.62, -6.12) * mm, "mid": v(49.74, -5.09) * mm, "end": v(49.83, -4.05) * mm});
            skArc(sketch, "E47.trimOffspring", {"start": v(48.96, -10.15) * mm, "mid": v(49.16, -9.13) * mm, "end": v(49.34, -8.1) * mm});
            skArc(sketch, "E48.trimOffspring", {"start": v(47.97, -14.1) * mm, "mid": v(48.25, -13.1) * mm, "end": v(48.51, -12.1) * mm});
            skArc(sketch, "E49.trimOffspring", {"start": v(46.66, -17.97) * mm, "mid": v(47.02, -17) * mm, "end": v(47.36, -16.01) * mm});
            skArc(sketch, "E50.trimOffspring", {"start": v(45.04, -21.7) * mm, "mid": v(45.48, -20.77) * mm, "end": v(45.9, -19.82) * mm});
            skArc(sketch, "E51.trimOffspring", {"start": v(43.12, -25.3) * mm, "mid": v(43.64, -24.4) * mm, "end": v(44.13, -23.5) * mm});
            skArc(sketch, "E52.trimOffspring", {"start": v(40.91, -28.74) * mm, "mid": v(41.5, -27.88) * mm, "end": v(42.07, -27.01) * mm});
            skArc(sketch, "E53.trimOffspring", {"start": v(38.43, -31.98) * mm, "mid": v(39.09, -31.17) * mm, "end": v(39.73, -30.35) * mm});
            skArc(sketch, "E54.trimOffspring", {"start": v(35.7, -35) * mm, "mid": v(36.42, -34.25) * mm, "end": v(37.12, -33.49) * mm});
            skArc(sketch, "E55.trimOffspring", {"start": v(32.73, -37.8) * mm, "mid": v(33.5, -37.1) * mm, "end": v(34.27, -36.4) * mm});
            skArc(sketch, "E56.trimOffspring", {"start": v(29.54, -40.34) * mm, "mid": v(30.37, -39.72) * mm, "end": v(31.19, -39.08) * mm});
            skArc(sketch, "E57.trimOffspring", {"start": v(26.15, -42.61) * mm, "mid": v(27.03, -42.06) * mm, "end": v(27.9, -41.49) * mm});
            skArc(sketch, "E58.trimOffspring", {"start": v(22.59, -44.6) * mm, "mid": v(23.51, -44.12) * mm, "end": v(24.42, -43.62) * mm});
            skArc(sketch, "E59.trimOffspring", {"start": v(18.88, -46.3) * mm, "mid": v(19.84, -45.9) * mm, "end": v(20.79, -45.47) * mm});
            skArc(sketch, "E60.trimOffspring", {"start": v(15.04, -47.68) * mm, "mid": v(16.03, -47.36) * mm, "end": v(17.01, -47.01) * mm});
            skArc(sketch, "E61.trimOffspring", {"start": v(11.1, -48.75) * mm, "mid": v(12.12, -48.5) * mm, "end": v(13.12, -48.24) * mm});
            skArc(sketch, "E62.trimOffspring", {"start": v(7.1, -49.49) * mm, "mid": v(8.12, -49.33) * mm, "end": v(9.15, -49.15) * mm});
            skArc(sketch, "E63.trimOffspring", {"start": v(3.04, -49.9) * mm, "mid": v(4.08, -49.83) * mm, "end": v(5.11, -49.73) * mm});
            skArc(sketch, "E64.trimOffspring", {"start": v(-1.04, -49.98) * mm, "mid": v(0, -50) * mm, "end": v(1.04, -49.98) * mm});
            skArc(sketch, "E65.trimOffspring", {"start": v(-5.11, -49.73) * mm, "mid": v(-4.08, -49.83) * mm, "end": v(-3.04, -49.9) * mm});
            skArc(sketch, "E66.trimOffspring", {"start": v(-9.15, -49.15) * mm, "mid": v(-8.12, -49.33) * mm, "end": v(-7.1, -49.49) * mm});
            skArc(sketch, "E67.trimOffspring", {"start": v(-13.12, -48.24) * mm, "mid": v(-12.12, -48.5) * mm, "end": v(-11.1, -48.75) * mm});
            skArc(sketch, "E68.trimOffspring", {"start": v(-17.01, -47.01) * mm, "mid": v(-16.03, -47.36) * mm, "end": v(-15.04, -47.68) * mm});
            skArc(sketch, "E69.trimOffspring", {"start": v(-20.79, -45.47) * mm, "mid": v(-19.84, -45.9) * mm, "end": v(-18.88, -46.3) * mm});
            skArc(sketch, "E70.trimOffspring", {"start": v(-24.43, -43.62) * mm, "mid": v(-23.51, -44.12) * mm, "end": v(-22.6, -44.6) * mm});
            skArc(sketch, "E71.trimOffspring", {"start": v(-27.9, -41.49) * mm, "mid": v(-27.03, -42.06) * mm, "end": v(-26.15, -42.61) * mm});
            skArc(sketch, "E72.trimOffspring", {"start": v(-31.19, -39.08) * mm, "mid": v(-30.37, -39.72) * mm, "end": v(-29.54, -40.34) * mm});
            skArc(sketch, "E73.trimOffspring", {"start": v(-48.51, -12.1) * mm, "mid": v(-48.25, -13.1) * mm, "end": v(-47.97, -14.1) * mm});
            skArc(sketch, "E74.trimOffspring", {"start": v(-47.36, -16.01) * mm, "mid": v(-47.02, -17) * mm, "end": v(-46.66, -17.97) * mm});
            skArc(sketch, "E75.trimOffspring", {"start": v(-45.9, -19.82) * mm, "mid": v(-45.48, -20.77) * mm, "end": v(-45.04, -21.7) * mm});
            skArc(sketch, "E76.trimOffspring", {"start": v(-44.13, -23.5) * mm, "mid": v(-43.64, -24.4) * mm, "end": v(-43.12, -25.3) * mm});
            skArc(sketch, "E77.trimOffspring", {"start": v(-42.07, -27.01) * mm, "mid": v(-41.5, -27.88) * mm, "end": v(-40.91, -28.74) * mm});
            skArc(sketch, "E78.trimOffspring", {"start": v(-39.73, -30.35) * mm, "mid": v(-39.1, -31.17) * mm, "end": v(-38.43, -31.98) * mm});
            skArc(sketch, "E79.trimOffspring", {"start": v(-37.12, -33.49) * mm, "mid": v(-36.42, -34.25) * mm, "end": v(-35.7, -35) * mm});
            skArc(sketch, "E80.trimOffspring", {"start": v(-34.27, -36.4) * mm, "mid": v(-33.5, -37.1) * mm, "end": v(-32.73, -37.8) * mm});
            skCircle(sketch, "E81", {"center": v(0, 0) * mm, "radius": 2.5 * mm});
            skArc(sketch, "E82", {"start": v(-2, 47.46) * mm, "mid": v(-41.14, 23.75) * mm, "end": v(-42.1, -22) * mm});
            skLineSegment(sketch, "E83", {"start": v(-2, 4.58) * mm, "end": v(-2, 47.46) * mm});
            skLineSegment(sketch, "E84", {"start": v(2, 4.58) * mm, "end": v(2, 47.46) * mm});
            skLineSegment(sketch, "E85.1.0", {"start": v(-4.97, -0.56) * mm, "end": v(-42.1, -22) * mm});
            skLineSegment(sketch, "E85.1.1", {"start": v(-2.97, -4.02) * mm, "end": v(-40.1, -25.46) * mm});
            skLineSegment(sketch, "E85.2.0", {"start": v(2.97, -4.02) * mm, "end": v(40.1, -25.46) * mm});
            skLineSegment(sketch, "E85.2.1", {"start": v(4.97, -0.56) * mm, "end": v(42.1, -22) * mm});
            skArc(sketch, "E86.trimOffspring", {"start": v(-40.1, -25.46) * mm, "mid": v(0, -47.5) * mm, "end": v(40.1, -25.46) * mm});
            skArc(sketch, "E87.trimOffspring", {"start": v(42.1, -22) * mm, "mid": v(41.14, 23.75) * mm, "end": v(2, 47.46) * mm});
            skArc(sketch, "E88", {"start": v(-2.97, -4.02) * mm, "mid": v(0, -5) * mm, "end": v(2.97, -4.02) * mm});
            skArc(sketch, "E89.trimOffspring", {"start": v(4.97, -0.56) * mm, "mid": v(4.33, 2.5) * mm, "end": v(2, 4.58) * mm});
            skArc(sketch, "E90.trimOffspring", {"start": v(-2, 4.58) * mm, "mid": v(-4.33, 2.5) * mm, "end": v(-4.97, -0.56) * mm});
            skPoint(sketch, "E91.orphan", {"position": v(-2, 1.5) * mm});
            skPoint(sketch, "E92.orphan", {"position": v(-2.3, 0.98) * mm});
            skPoint(sketch, "E93.orphan", {"position": v(-0.3, -2.48) * mm});
            skPoint(sketch, "E94.orphan", {"position": v(0.3, -2.48) * mm});
            skPoint(sketch, "E95.orphan", {"position": v(2.3, 0.98) * mm});
            skPoint(sketch, "E96.orphan", {"position": v(2, 1.5) * mm});
            skArc(sketch, "E97.trimOffspring", {"start": v(-5.07, 49.74) * mm, "mid": v(-6.1, 49.63) * mm, "end": v(-7.14, 49.49) * mm});
            skArc(sketch, "E98.trimOffspring", {"start": v(-42.05, 27.05) * mm, "mid": v(-42.6, 26.17) * mm, "end": v(-43.14, 25.28) * mm});
            skSolve(sketch);
        }
        {
            var Q0;
            Q0=makeQuery(id+"F0.imprint","IMPRINT",FACE,{"disambiguationData":[TD([[makeQuery(id+"F0.imprint","IMPRINT",EDGE,{"derivedFrom":sQuery(id+"F0.wireOp",EDGE,"E0")}),1.0]])]});
            var Q1;
            Q1=makeQuery(id+"F0.imprint","IMPRINT",FACE,{"disambiguationData":[TD([[makeQuery(id+"F0.imprint","IMPRINT",EDGE,{"derivedFrom":sQuery(id+"F0.wireOp",EDGE,"E1")}),-1.0]])]});
            extrude(context, id + "F1", {"entities" : qUnion([Q0, Q1]), "depth" : 15 * mm, "offsetDistance" : 25 * mm});
        }
        {
            var Q0;
            Q0=makeQuery(id+"F1.opExtrude","SWEPT_EDGE",EDGE,{"disambiguationData":[OSD([sQuery(id+"F0.wireOp",EDGE,"E1"),sQuery(id+"F0.wireOp",EDGE,"E2")])]});
            var Q1;
            Q1=makeQuery(id+"F1.opExtrude","SWEPT_EDGE",EDGE,{"disambiguationData":[OSD([sQuery(id+"F0.wireOp",EDGE,"E2"),sQuery(id+"F0.wireOp",EDGE,"E3")])]});
            var Q2;
            Q2=makeQuery(id+"F1.opExtrude","SWEPT_EDGE",EDGE,{"disambiguationData":[OSD([sQuery(id+"F0.wireOp",EDGE,"E4.76.0"),sQuery(id+"F0.wireOp",EDGE,"E4.76.2")])]});
            var Q3;
            Q3=makeQuery(id+"F1.opExtrude","SWEPT_EDGE",EDGE,{"disambiguationData":[OSD([sQuery(id+"F0.wireOp",EDGE,"E4.75.0"),sQuery(id+"F0.wireOp",EDGE,"E4.75.2")])]});
            var Q4;
            Q4=makeQuery(id+"F1.opExtrude","SWEPT_EDGE",EDGE,{"disambiguationData":[OSD([sQuery(id+"F0.wireOp",EDGE,"E4.75.0"),sQuery(id+"F0.wireOp",EDGE,"E4.75.1")])]});
            var Q5;
            Q5=makeQuery(id+"F1.opExtrude","SWEPT_EDGE",EDGE,{"disambiguationData":[OSD([sQuery(id+"F0.wireOp",EDGE,"E4.1.0"),sQuery(id+"F0.wireOp",EDGE,"E4.1.1")])]});
            var Q6;
            Q6=makeQuery(id+"F1.opExtrude","SWEPT_EDGE",EDGE,{"disambiguationData":[OSD([sQuery(id+"F0.wireOp",EDGE,"E4.1.0"),sQuery(id+"F0.wireOp",EDGE,"E4.1.2")])]});
            var Q7;
            Q7=makeQuery(id+"F1.opExtrude","SWEPT_EDGE",EDGE,{"disambiguationData":[OSD([sQuery(id+"F0.wireOp",EDGE,"E4.2.0"),sQuery(id+"F0.wireOp",EDGE,"E4.2.1")])]});
            var Q8;
            Q8=makeQuery(id+"F1.opExtrude","SWEPT_EDGE",EDGE,{"disambiguationData":[OSD([sQuery(id+"F0.wireOp",EDGE,"E4.2.0"),sQuery(id+"F0.wireOp",EDGE,"E4.2.2")])]});
            var Q9;
            Q9=makeQuery(id+"F1.opExtrude","SWEPT_EDGE",EDGE,{"disambiguationData":[OSD([sQuery(id+"F0.wireOp",EDGE,"E4.3.0"),sQuery(id+"F0.wireOp",EDGE,"E4.3.1")])]});
            var Q10;
            Q10=makeQuery(id+"F1.opExtrude","SWEPT_EDGE",EDGE,{"disambiguationData":[OSD([sQuery(id+"F0.wireOp",EDGE,"E4.3.0"),sQuery(id+"F0.wireOp",EDGE,"E4.3.2")])]});
            var Q11;
            Q11=makeQuery(id+"F1.opExtrude","SWEPT_EDGE",EDGE,{"disambiguationData":[OSD([sQuery(id+"F0.wireOp",EDGE,"E4.4.0"),sQuery(id+"F0.wireOp",EDGE,"E4.4.1")])]});
            var Q12;
            Q12=makeQuery(id+"F1.opExtrude","SWEPT_EDGE",EDGE,{"disambiguationData":[OSD([sQuery(id+"F0.wireOp",EDGE,"E4.4.0"),sQuery(id+"F0.wireOp",EDGE,"E4.4.2")])]});
            var Q13;
            Q13=makeQuery(id+"F1.opExtrude","SWEPT_EDGE",EDGE,{"disambiguationData":[OSD([sQuery(id+"F0.wireOp",EDGE,"E4.5.0"),sQuery(id+"F0.wireOp",EDGE,"E4.5.1")])]});
            var Q14;
            Q14=makeQuery(id+"F1.opExtrude","SWEPT_EDGE",EDGE,{"disambiguationData":[OSD([sQuery(id+"F0.wireOp",EDGE,"E4.5.0"),sQuery(id+"F0.wireOp",EDGE,"E4.5.2")])]});
            var Q15;
            Q15=makeQuery(id+"F1.opExtrude","SWEPT_EDGE",EDGE,{"disambiguationData":[OSD([sQuery(id+"F0.wireOp",EDGE,"E4.6.0"),sQuery(id+"F0.wireOp",EDGE,"E4.6.1")])]});
            var Q16;
            Q16=makeQuery(id+"F1.opExtrude","SWEPT_EDGE",EDGE,{"disambiguationData":[OSD([sQuery(id+"F0.wireOp",EDGE,"E4.7.0"),sQuery(id+"F0.wireOp",EDGE,"E4.7.1")])]});
            var Q17;
            Q17=makeQuery(id+"F1.opExtrude","SWEPT_EDGE",EDGE,{"disambiguationData":[OSD([sQuery(id+"F0.wireOp",EDGE,"E4.7.0"),sQuery(id+"F0.wireOp",EDGE,"E4.7.2")])]});
            var Q18;
            Q18=makeQuery(id+"F1.opExtrude","SWEPT_EDGE",EDGE,{"disambiguationData":[OSD([sQuery(id+"F0.wireOp",EDGE,"E4.6.0"),sQuery(id+"F0.wireOp",EDGE,"E4.6.2")])]});
            var Q19;
            Q19=makeQuery(id+"F1.opExtrude","SWEPT_EDGE",EDGE,{"disambiguationData":[OSD([sQuery(id+"F0.wireOp",EDGE,"E4.8.0"),sQuery(id+"F0.wireOp",EDGE,"E4.8.2")])]});
            var Q20;
            Q20=makeQuery(id+"F1.opExtrude","SWEPT_EDGE",EDGE,{"disambiguationData":[OSD([sQuery(id+"F0.wireOp",EDGE,"E4.8.0"),sQuery(id+"F0.wireOp",EDGE,"E4.8.1")])]});
            var Q21;
            Q21=makeQuery(id+"F1.opExtrude","SWEPT_EDGE",EDGE,{"disambiguationData":[OSD([sQuery(id+"F0.wireOp",EDGE,"E4.9.0"),sQuery(id+"F0.wireOp",EDGE,"E4.9.1")])]});
            var Q22;
            Q22=makeQuery(id+"F1.opExtrude","SWEPT_EDGE",EDGE,{"disambiguationData":[OSD([sQuery(id+"F0.wireOp",EDGE,"E4.9.0"),sQuery(id+"F0.wireOp",EDGE,"E4.9.2")])]});
            var Q23;
            Q23=makeQuery(id+"F1.opExtrude","SWEPT_EDGE",EDGE,{"disambiguationData":[OSD([sQuery(id+"F0.wireOp",EDGE,"E4.10.0"),sQuery(id+"F0.wireOp",EDGE,"E4.10.1")])]});
            var Q24;
            Q24=makeQuery(id+"F1.opExtrude","SWEPT_EDGE",EDGE,{"disambiguationData":[OSD([sQuery(id+"F0.wireOp",EDGE,"E4.10.0"),sQuery(id+"F0.wireOp",EDGE,"E4.10.2")])]});
            var Q25;
            Q25=makeQuery(id+"F1.opExtrude","SWEPT_EDGE",EDGE,{"disambiguationData":[OSD([sQuery(id+"F0.wireOp",EDGE,"E4.11.0"),sQuery(id+"F0.wireOp",EDGE,"E4.11.1")])]});
            var Q26;
            Q26=makeQuery(id+"F1.opExtrude","SWEPT_EDGE",EDGE,{"disambiguationData":[OSD([sQuery(id+"F0.wireOp",EDGE,"E4.11.0"),sQuery(id+"F0.wireOp",EDGE,"E4.11.2")])]});
            var Q27;
            Q27=makeQuery(id+"F1.opExtrude","SWEPT_EDGE",EDGE,{"disambiguationData":[OSD([sQuery(id+"F0.wireOp",EDGE,"E4.12.0"),sQuery(id+"F0.wireOp",EDGE,"E4.12.1")])]});
            var Q28;
            Q28=makeQuery(id+"F1.opExtrude","SWEPT_EDGE",EDGE,{"disambiguationData":[OSD([sQuery(id+"F0.wireOp",EDGE,"E4.12.0"),sQuery(id+"F0.wireOp",EDGE,"E4.12.2")])]});
            var Q29;
            Q29=makeQuery(id+"F1.opExtrude","SWEPT_EDGE",EDGE,{"disambiguationData":[OSD([sQuery(id+"F0.wireOp",EDGE,"E4.13.0"),sQuery(id+"F0.wireOp",EDGE,"E4.13.1")])]});
            var Q30;
            Q30=makeQuery(id+"F1.opExtrude","SWEPT_EDGE",EDGE,{"disambiguationData":[OSD([sQuery(id+"F0.wireOp",EDGE,"E4.13.0"),sQuery(id+"F0.wireOp",EDGE,"E4.13.2")])]});
            var Q31;
            Q31=makeQuery(id+"F1.opExtrude","SWEPT_EDGE",EDGE,{"disambiguationData":[OSD([sQuery(id+"F0.wireOp",EDGE,"E4.14.0"),sQuery(id+"F0.wireOp",EDGE,"E4.14.1")])]});
            var Q32;
            Q32=makeQuery(id+"F1.opExtrude","SWEPT_EDGE",EDGE,{"disambiguationData":[OSD([sQuery(id+"F0.wireOp",EDGE,"E4.14.0"),sQuery(id+"F0.wireOp",EDGE,"E4.14.2")])]});
            var Q33;
            Q33=makeQuery(id+"F1.opExtrude","SWEPT_EDGE",EDGE,{"disambiguationData":[OSD([sQuery(id+"F0.wireOp",EDGE,"E4.15.0"),sQuery(id+"F0.wireOp",EDGE,"E4.15.1")])]});
            var Q34;
            Q34=makeQuery(id+"F1.opExtrude","SWEPT_EDGE",EDGE,{"disambiguationData":[OSD([sQuery(id+"F0.wireOp",EDGE,"E4.15.0"),sQuery(id+"F0.wireOp",EDGE,"E4.15.2")])]});
            var Q35;
            Q35=makeQuery(id+"F1.opExtrude","SWEPT_EDGE",EDGE,{"disambiguationData":[OSD([sQuery(id+"F0.wireOp",EDGE,"E4.16.0"),sQuery(id+"F0.wireOp",EDGE,"E4.16.1")])]});
            var Q36;
            Q36=makeQuery(id+"F1.opExtrude","SWEPT_EDGE",EDGE,{"disambiguationData":[OSD([sQuery(id+"F0.wireOp",EDGE,"E4.16.0"),sQuery(id+"F0.wireOp",EDGE,"E4.16.2")])]});
            var Q37;
            Q37=makeQuery(id+"F1.opExtrude","SWEPT_EDGE",EDGE,{"disambiguationData":[OSD([sQuery(id+"F0.wireOp",EDGE,"E4.17.0"),sQuery(id+"F0.wireOp",EDGE,"E4.17.1")])]});
            var Q38;
            Q38=makeQuery(id+"F1.opExtrude","SWEPT_EDGE",EDGE,{"disambiguationData":[OSD([sQuery(id+"F0.wireOp",EDGE,"E4.17.0"),sQuery(id+"F0.wireOp",EDGE,"E4.17.2")])]});
            var Q39;
            Q39=makeQuery(id+"F1.opExtrude","SWEPT_EDGE",EDGE,{"disambiguationData":[OSD([sQuery(id+"F0.wireOp",EDGE,"E4.18.0"),sQuery(id+"F0.wireOp",EDGE,"E4.18.1")])]});
            var Q40;
            Q40=makeQuery(id+"F1.opExtrude","SWEPT_EDGE",EDGE,{"disambiguationData":[OSD([sQuery(id+"F0.wireOp",EDGE,"E4.18.0"),sQuery(id+"F0.wireOp",EDGE,"E4.18.2")])]});
            var Q41;
            Q41=makeQuery(id+"F1.opExtrude","SWEPT_EDGE",EDGE,{"disambiguationData":[OSD([sQuery(id+"F0.wireOp",EDGE,"E4.19.0"),sQuery(id+"F0.wireOp",EDGE,"E4.19.1")])]});
            var Q42;
            Q42=makeQuery(id+"F1.opExtrude","SWEPT_EDGE",EDGE,{"disambiguationData":[OSD([sQuery(id+"F0.wireOp",EDGE,"E4.19.0"),sQuery(id+"F0.wireOp",EDGE,"E4.19.2")])]});
            var Q43;
            Q43=makeQuery(id+"F1.opExtrude","SWEPT_EDGE",EDGE,{"disambiguationData":[OSD([sQuery(id+"F0.wireOp",EDGE,"E4.20.0"),sQuery(id+"F0.wireOp",EDGE,"E4.20.1")])]});
            var Q44;
            Q44=makeQuery(id+"F1.opExtrude","SWEPT_EDGE",EDGE,{"disambiguationData":[OSD([sQuery(id+"F0.wireOp",EDGE,"E4.20.0"),sQuery(id+"F0.wireOp",EDGE,"E4.20.2")])]});
            var Q45;
            Q45=makeQuery(id+"F1.opExtrude","SWEPT_EDGE",EDGE,{"disambiguationData":[OSD([sQuery(id+"F0.wireOp",EDGE,"E4.21.0"),sQuery(id+"F0.wireOp",EDGE,"E4.21.1")])]});
            var Q46;
            Q46=makeQuery(id+"F1.opExtrude","SWEPT_EDGE",EDGE,{"disambiguationData":[OSD([sQuery(id+"F0.wireOp",EDGE,"E4.21.0"),sQuery(id+"F0.wireOp",EDGE,"E4.21.2")])]});
            var Q47;
            Q47=makeQuery(id+"F1.opExtrude","SWEPT_EDGE",EDGE,{"disambiguationData":[OSD([sQuery(id+"F0.wireOp",EDGE,"E4.22.0"),sQuery(id+"F0.wireOp",EDGE,"E4.22.1")])]});
            var Q48;
            Q48=makeQuery(id+"F1.opExtrude","SWEPT_EDGE",EDGE,{"disambiguationData":[OSD([sQuery(id+"F0.wireOp",EDGE,"E4.22.0"),sQuery(id+"F0.wireOp",EDGE,"E4.22.2")])]});
            var Q49;
            Q49=makeQuery(id+"F1.opExtrude","SWEPT_EDGE",EDGE,{"disambiguationData":[OSD([sQuery(id+"F0.wireOp",EDGE,"E4.23.0"),sQuery(id+"F0.wireOp",EDGE,"E4.23.1")])]});
            var Q50;
            Q50=makeQuery(id+"F1.opExtrude","SWEPT_EDGE",EDGE,{"disambiguationData":[OSD([sQuery(id+"F0.wireOp",EDGE,"E4.23.0"),sQuery(id+"F0.wireOp",EDGE,"E4.23.2")])]});
            var Q51;
            Q51=makeQuery(id+"F1.opExtrude","SWEPT_EDGE",EDGE,{"disambiguationData":[OSD([sQuery(id+"F0.wireOp",EDGE,"E4.24.0"),sQuery(id+"F0.wireOp",EDGE,"E4.24.1")])]});
            var Q52;
            Q52=makeQuery(id+"F1.opExtrude","SWEPT_EDGE",EDGE,{"disambiguationData":[OSD([sQuery(id+"F0.wireOp",EDGE,"E4.24.0"),sQuery(id+"F0.wireOp",EDGE,"E4.24.2")])]});
            var Q53;
            Q53=makeQuery(id+"F1.opExtrude","SWEPT_EDGE",EDGE,{"disambiguationData":[OSD([sQuery(id+"F0.wireOp",EDGE,"E4.25.0"),sQuery(id+"F0.wireOp",EDGE,"E4.25.1")])]});
            var Q54;
            Q54=makeQuery(id+"F1.opExtrude","SWEPT_EDGE",EDGE,{"disambiguationData":[OSD([sQuery(id+"F0.wireOp",EDGE,"E4.25.0"),sQuery(id+"F0.wireOp",EDGE,"E4.25.2")])]});
            var Q55;
            Q55=makeQuery(id+"F1.opExtrude","SWEPT_EDGE",EDGE,{"disambiguationData":[OSD([sQuery(id+"F0.wireOp",EDGE,"E4.26.0"),sQuery(id+"F0.wireOp",EDGE,"E4.26.1")])]});
            var Q56;
            Q56=makeQuery(id+"F1.opExtrude","SWEPT_EDGE",EDGE,{"disambiguationData":[OSD([sQuery(id+"F0.wireOp",EDGE,"E4.26.0"),sQuery(id+"F0.wireOp",EDGE,"E4.26.2")])]});
            var Q57;
            Q57=makeQuery(id+"F1.opExtrude","SWEPT_EDGE",EDGE,{"disambiguationData":[OSD([sQuery(id+"F0.wireOp",EDGE,"E4.27.0"),sQuery(id+"F0.wireOp",EDGE,"E4.27.1")])]});
            var Q58;
            Q58=makeQuery(id+"F1.opExtrude","SWEPT_EDGE",EDGE,{"disambiguationData":[OSD([sQuery(id+"F0.wireOp",EDGE,"E4.27.0"),sQuery(id+"F0.wireOp",EDGE,"E4.27.2")])]});
            var Q59;
            Q59=makeQuery(id+"F1.opExtrude","SWEPT_EDGE",EDGE,{"disambiguationData":[OSD([sQuery(id+"F0.wireOp",EDGE,"E4.28.0"),sQuery(id+"F0.wireOp",EDGE,"E4.28.1")])]});
            var Q60;
            Q60=makeQuery(id+"F1.opExtrude","SWEPT_EDGE",EDGE,{"disambiguationData":[OSD([sQuery(id+"F0.wireOp",EDGE,"E4.28.0"),sQuery(id+"F0.wireOp",EDGE,"E4.28.2")])]});
            var Q61;
            Q61=makeQuery(id+"F1.opExtrude","SWEPT_EDGE",EDGE,{"disambiguationData":[OSD([sQuery(id+"F0.wireOp",EDGE,"E4.29.0"),sQuery(id+"F0.wireOp",EDGE,"E4.29.1")])]});
            var Q62;
            Q62=makeQuery(id+"F1.opExtrude","SWEPT_EDGE",EDGE,{"disambiguationData":[OSD([sQuery(id+"F0.wireOp",EDGE,"E4.29.0"),sQuery(id+"F0.wireOp",EDGE,"E4.29.2")])]});
            var Q63;
            Q63=makeQuery(id+"F1.opExtrude","SWEPT_EDGE",EDGE,{"disambiguationData":[OSD([sQuery(id+"F0.wireOp",EDGE,"E4.30.0"),sQuery(id+"F0.wireOp",EDGE,"E4.30.1")])]});
            var Q64;
            Q64=makeQuery(id+"F1.opExtrude","SWEPT_EDGE",EDGE,{"disambiguationData":[OSD([sQuery(id+"F0.wireOp",EDGE,"E4.30.0"),sQuery(id+"F0.wireOp",EDGE,"E4.30.2")])]});
            var Q65;
            Q65=makeQuery(id+"F1.opExtrude","SWEPT_EDGE",EDGE,{"disambiguationData":[OSD([sQuery(id+"F0.wireOp",EDGE,"E4.31.0"),sQuery(id+"F0.wireOp",EDGE,"E4.31.1")])]});
            var Q66;
            Q66=makeQuery(id+"F1.opExtrude","SWEPT_EDGE",EDGE,{"disambiguationData":[OSD([sQuery(id+"F0.wireOp",EDGE,"E4.31.0"),sQuery(id+"F0.wireOp",EDGE,"E4.31.2")])]});
            var Q67;
            Q67=makeQuery(id+"F1.opExtrude","SWEPT_EDGE",EDGE,{"disambiguationData":[OSD([sQuery(id+"F0.wireOp",EDGE,"E4.32.0"),sQuery(id+"F0.wireOp",EDGE,"E4.32.1")])]});
            var Q68;
            Q68=makeQuery(id+"F1.opExtrude","SWEPT_EDGE",EDGE,{"disambiguationData":[OSD([sQuery(id+"F0.wireOp",EDGE,"E4.32.0"),sQuery(id+"F0.wireOp",EDGE,"E4.32.2")])]});
            var Q69;
            Q69=makeQuery(id+"F1.opExtrude","SWEPT_EDGE",EDGE,{"disambiguationData":[OSD([sQuery(id+"F0.wireOp",EDGE,"E4.33.0"),sQuery(id+"F0.wireOp",EDGE,"E4.33.1")])]});
            var Q70;
            Q70=makeQuery(id+"F1.opExtrude","SWEPT_EDGE",EDGE,{"disambiguationData":[OSD([sQuery(id+"F0.wireOp",EDGE,"E4.33.0"),sQuery(id+"F0.wireOp",EDGE,"E4.33.2")])]});
            var Q71;
            Q71=makeQuery(id+"F1.opExtrude","SWEPT_EDGE",EDGE,{"disambiguationData":[OSD([sQuery(id+"F0.wireOp",EDGE,"E4.34.0"),sQuery(id+"F0.wireOp",EDGE,"E4.34.1")])]});
            var Q72;
            Q72=makeQuery(id+"F1.opExtrude","SWEPT_EDGE",EDGE,{"disambiguationData":[OSD([sQuery(id+"F0.wireOp",EDGE,"E4.34.0"),sQuery(id+"F0.wireOp",EDGE,"E4.34.2")])]});
            var Q73;
            Q73=makeQuery(id+"F1.opExtrude","SWEPT_EDGE",EDGE,{"disambiguationData":[OSD([sQuery(id+"F0.wireOp",EDGE,"E4.35.0"),sQuery(id+"F0.wireOp",EDGE,"E4.35.1")])]});
            var Q74;
            Q74=makeQuery(id+"F1.opExtrude","SWEPT_EDGE",EDGE,{"disambiguationData":[OSD([sQuery(id+"F0.wireOp",EDGE,"E4.35.0"),sQuery(id+"F0.wireOp",EDGE,"E4.35.2")])]});
            var Q75;
            Q75=makeQuery(id+"F1.opExtrude","SWEPT_EDGE",EDGE,{"disambiguationData":[OSD([sQuery(id+"F0.wireOp",EDGE,"E4.36.0"),sQuery(id+"F0.wireOp",EDGE,"E4.36.1")])]});
            var Q76;
            Q76=makeQuery(id+"F1.opExtrude","SWEPT_EDGE",EDGE,{"disambiguationData":[OSD([sQuery(id+"F0.wireOp",EDGE,"E4.36.0"),sQuery(id+"F0.wireOp",EDGE,"E4.36.2")])]});
            var Q77;
            Q77=makeQuery(id+"F1.opExtrude","SWEPT_EDGE",EDGE,{"disambiguationData":[OSD([sQuery(id+"F0.wireOp",EDGE,"E4.38.0"),sQuery(id+"F0.wireOp",EDGE,"E4.38.1")])]});
            var Q78;
            Q78=makeQuery(id+"F1.opExtrude","SWEPT_EDGE",EDGE,{"disambiguationData":[OSD([sQuery(id+"F0.wireOp",EDGE,"E4.37.0"),sQuery(id+"F0.wireOp",EDGE,"E4.37.1")])]});
            var Q79;
            Q79=makeQuery(id+"F1.opExtrude","SWEPT_EDGE",EDGE,{"disambiguationData":[OSD([sQuery(id+"F0.wireOp",EDGE,"E4.38.0"),sQuery(id+"F0.wireOp",EDGE,"E4.38.2")])]});
            var Q80;
            Q80=makeQuery(id+"F1.opExtrude","SWEPT_EDGE",EDGE,{"disambiguationData":[OSD([sQuery(id+"F0.wireOp",EDGE,"E4.39.0"),sQuery(id+"F0.wireOp",EDGE,"E4.39.1")])]});
            var Q81;
            Q81=makeQuery(id+"F1.opExtrude","SWEPT_EDGE",EDGE,{"disambiguationData":[OSD([sQuery(id+"F0.wireOp",EDGE,"E4.37.0"),sQuery(id+"F0.wireOp",EDGE,"E4.37.2")])]});
            var Q82;
            Q82=makeQuery(id+"F1.opExtrude","SWEPT_EDGE",EDGE,{"disambiguationData":[OSD([sQuery(id+"F0.wireOp",EDGE,"E4.39.0"),sQuery(id+"F0.wireOp",EDGE,"E4.39.2")])]});
            var Q83;
            Q83=makeQuery(id+"F1.opExtrude","SWEPT_EDGE",EDGE,{"disambiguationData":[OSD([sQuery(id+"F0.wireOp",EDGE,"E4.40.0"),sQuery(id+"F0.wireOp",EDGE,"E4.40.1")])]});
            var Q84;
            Q84=makeQuery(id+"F1.opExtrude","SWEPT_EDGE",EDGE,{"disambiguationData":[OSD([sQuery(id+"F0.wireOp",EDGE,"E4.40.0"),sQuery(id+"F0.wireOp",EDGE,"E4.40.2")])]});
            var Q85;
            Q85=makeQuery(id+"F1.opExtrude","SWEPT_EDGE",EDGE,{"disambiguationData":[OSD([sQuery(id+"F0.wireOp",EDGE,"E4.41.0"),sQuery(id+"F0.wireOp",EDGE,"E4.41.1")])]});
            var Q86;
            Q86=makeQuery(id+"F1.opExtrude","SWEPT_EDGE",EDGE,{"disambiguationData":[OSD([sQuery(id+"F0.wireOp",EDGE,"E4.41.0"),sQuery(id+"F0.wireOp",EDGE,"E4.41.2")])]});
            var Q87;
            Q87=makeQuery(id+"F1.opExtrude","SWEPT_EDGE",EDGE,{"disambiguationData":[OSD([sQuery(id+"F0.wireOp",EDGE,"E4.42.0"),sQuery(id+"F0.wireOp",EDGE,"E4.42.1")])]});
            var Q88;
            Q88=makeQuery(id+"F1.opExtrude","SWEPT_EDGE",EDGE,{"disambiguationData":[OSD([sQuery(id+"F0.wireOp",EDGE,"E4.42.0"),sQuery(id+"F0.wireOp",EDGE,"E4.42.2")])]});
            var Q89;
            Q89=makeQuery(id+"F1.opExtrude","SWEPT_EDGE",EDGE,{"disambiguationData":[OSD([sQuery(id+"F0.wireOp",EDGE,"E4.43.0"),sQuery(id+"F0.wireOp",EDGE,"E4.43.1")])]});
            var Q90;
            Q90=makeQuery(id+"F1.opExtrude","SWEPT_EDGE",EDGE,{"disambiguationData":[OSD([sQuery(id+"F0.wireOp",EDGE,"E4.43.0"),sQuery(id+"F0.wireOp",EDGE,"E4.43.2")])]});
            var Q91;
            Q91=makeQuery(id+"F1.opExtrude","SWEPT_EDGE",EDGE,{"disambiguationData":[OSD([sQuery(id+"F0.wireOp",EDGE,"E4.44.0"),sQuery(id+"F0.wireOp",EDGE,"E4.44.1")])]});
            var Q92;
            Q92=makeQuery(id+"F1.opExtrude","SWEPT_EDGE",EDGE,{"disambiguationData":[OSD([sQuery(id+"F0.wireOp",EDGE,"E4.44.0"),sQuery(id+"F0.wireOp",EDGE,"E4.44.2")])]});
            var Q93;
            Q93=makeQuery(id+"F1.opExtrude","SWEPT_EDGE",EDGE,{"disambiguationData":[OSD([sQuery(id+"F0.wireOp",EDGE,"E4.45.0"),sQuery(id+"F0.wireOp",EDGE,"E4.45.1")])]});
            var Q94;
            Q94=makeQuery(id+"F1.opExtrude","SWEPT_EDGE",EDGE,{"disambiguationData":[OSD([sQuery(id+"F0.wireOp",EDGE,"E4.45.0"),sQuery(id+"F0.wireOp",EDGE,"E4.45.2")])]});
            var Q95;
            Q95=makeQuery(id+"F1.opExtrude","SWEPT_EDGE",EDGE,{"disambiguationData":[OSD([sQuery(id+"F0.wireOp",EDGE,"E4.46.0"),sQuery(id+"F0.wireOp",EDGE,"E4.46.1")])]});
            var Q96;
            Q96=makeQuery(id+"F1.opExtrude","SWEPT_EDGE",EDGE,{"disambiguationData":[OSD([sQuery(id+"F0.wireOp",EDGE,"E4.46.0"),sQuery(id+"F0.wireOp",EDGE,"E4.46.2")])]});
            var Q97;
            Q97=makeQuery(id+"F1.opExtrude","SWEPT_EDGE",EDGE,{"disambiguationData":[OSD([sQuery(id+"F0.wireOp",EDGE,"E4.47.0"),sQuery(id+"F0.wireOp",EDGE,"E4.47.1")])]});
            var Q98;
            Q98=makeQuery(id+"F1.opExtrude","SWEPT_EDGE",EDGE,{"disambiguationData":[OSD([sQuery(id+"F0.wireOp",EDGE,"E4.47.0"),sQuery(id+"F0.wireOp",EDGE,"E4.47.2")])]});
            var Q99;
            Q99=makeQuery(id+"F1.opExtrude","SWEPT_EDGE",EDGE,{"disambiguationData":[OSD([sQuery(id+"F0.wireOp",EDGE,"E4.48.0"),sQuery(id+"F0.wireOp",EDGE,"E4.48.1")])]});
            var Q100;
            Q100=makeQuery(id+"F1.opExtrude","SWEPT_EDGE",EDGE,{"disambiguationData":[OSD([sQuery(id+"F0.wireOp",EDGE,"E4.48.0"),sQuery(id+"F0.wireOp",EDGE,"E4.48.2")])]});
            var Q101;
            Q101=makeQuery(id+"F1.opExtrude","SWEPT_EDGE",EDGE,{"disambiguationData":[OSD([sQuery(id+"F0.wireOp",EDGE,"E4.49.0"),sQuery(id+"F0.wireOp",EDGE,"E4.49.1")])]});
            var Q102;
            Q102=makeQuery(id+"F1.opExtrude","SWEPT_EDGE",EDGE,{"disambiguationData":[OSD([sQuery(id+"F0.wireOp",EDGE,"E4.49.0"),sQuery(id+"F0.wireOp",EDGE,"E4.49.2")])]});
            var Q103;
            Q103=makeQuery(id+"F1.opExtrude","SWEPT_EDGE",EDGE,{"disambiguationData":[OSD([sQuery(id+"F0.wireOp",EDGE,"E4.50.0"),sQuery(id+"F0.wireOp",EDGE,"E4.50.1")])]});
            var Q104;
            Q104=makeQuery(id+"F1.opExtrude","SWEPT_EDGE",EDGE,{"disambiguationData":[OSD([sQuery(id+"F0.wireOp",EDGE,"E4.50.0"),sQuery(id+"F0.wireOp",EDGE,"E4.50.2")])]});
            var Q105;
            Q105=makeQuery(id+"F1.opExtrude","SWEPT_EDGE",EDGE,{"disambiguationData":[OSD([sQuery(id+"F0.wireOp",EDGE,"E4.51.0"),sQuery(id+"F0.wireOp",EDGE,"E4.51.1")])]});
            var Q106;
            Q106=makeQuery(id+"F1.opExtrude","SWEPT_EDGE",EDGE,{"disambiguationData":[OSD([sQuery(id+"F0.wireOp",EDGE,"E4.51.0"),sQuery(id+"F0.wireOp",EDGE,"E4.51.2")])]});
            var Q107;
            Q107=makeQuery(id+"F1.opExtrude","SWEPT_EDGE",EDGE,{"disambiguationData":[OSD([sQuery(id+"F0.wireOp",EDGE,"E4.74.0"),sQuery(id+"F0.wireOp",EDGE,"E4.74.2")])]});
            var Q108;
            Q108=makeQuery(id+"F1.opExtrude","SWEPT_EDGE",EDGE,{"disambiguationData":[OSD([sQuery(id+"F0.wireOp",EDGE,"E4.74.0"),sQuery(id+"F0.wireOp",EDGE,"E4.74.1")])]});
            var Q109;
            Q109=makeQuery(id+"F1.opExtrude","SWEPT_EDGE",EDGE,{"disambiguationData":[OSD([sQuery(id+"F0.wireOp",EDGE,"E4.73.0"),sQuery(id+"F0.wireOp",EDGE,"E4.73.2")])]});
            var Q110;
            Q110=makeQuery(id+"F1.opExtrude","SWEPT_EDGE",EDGE,{"disambiguationData":[OSD([sQuery(id+"F0.wireOp",EDGE,"E4.73.0"),sQuery(id+"F0.wireOp",EDGE,"E4.73.1")])]});
            var Q111;
            Q111=makeQuery(id+"F1.opExtrude","SWEPT_EDGE",EDGE,{"disambiguationData":[OSD([sQuery(id+"F0.wireOp",EDGE,"E4.72.0"),sQuery(id+"F0.wireOp",EDGE,"E4.72.2")])]});
            var Q112;
            Q112=makeQuery(id+"F1.opExtrude","SWEPT_EDGE",EDGE,{"disambiguationData":[OSD([sQuery(id+"F0.wireOp",EDGE,"E4.72.0"),sQuery(id+"F0.wireOp",EDGE,"E4.72.1")])]});
            var Q113;
            Q113=makeQuery(id+"F1.opExtrude","SWEPT_EDGE",EDGE,{"disambiguationData":[OSD([sQuery(id+"F0.wireOp",EDGE,"E4.71.0"),sQuery(id+"F0.wireOp",EDGE,"E4.71.2")])]});
            var Q114;
            Q114=makeQuery(id+"F1.opExtrude","SWEPT_EDGE",EDGE,{"disambiguationData":[OSD([sQuery(id+"F0.wireOp",EDGE,"E4.71.0"),sQuery(id+"F0.wireOp",EDGE,"E4.71.1")])]});
            var Q115;
            Q115=makeQuery(id+"F1.opExtrude","SWEPT_EDGE",EDGE,{"disambiguationData":[OSD([sQuery(id+"F0.wireOp",EDGE,"E4.70.0"),sQuery(id+"F0.wireOp",EDGE,"E4.70.2")])]});
            var Q116;
            Q116=makeQuery(id+"F1.opExtrude","SWEPT_EDGE",EDGE,{"disambiguationData":[OSD([sQuery(id+"F0.wireOp",EDGE,"E4.70.0"),sQuery(id+"F0.wireOp",EDGE,"E4.70.1")])]});
            var Q117;
            Q117=makeQuery(id+"F1.opExtrude","SWEPT_EDGE",EDGE,{"disambiguationData":[OSD([sQuery(id+"F0.wireOp",EDGE,"E4.69.0"),sQuery(id+"F0.wireOp",EDGE,"E4.69.2")])]});
            var Q118;
            Q118=makeQuery(id+"F1.opExtrude","SWEPT_EDGE",EDGE,{"disambiguationData":[OSD([sQuery(id+"F0.wireOp",EDGE,"E4.69.0"),sQuery(id+"F0.wireOp",EDGE,"E4.69.1")])]});
            var Q119;
            Q119=makeQuery(id+"F1.opExtrude","SWEPT_EDGE",EDGE,{"disambiguationData":[OSD([sQuery(id+"F0.wireOp",EDGE,"E4.68.0"),sQuery(id+"F0.wireOp",EDGE,"E4.68.2")])]});
            var Q120;
            Q120=makeQuery(id+"F1.opExtrude","SWEPT_EDGE",EDGE,{"disambiguationData":[OSD([sQuery(id+"F0.wireOp",EDGE,"E4.68.0"),sQuery(id+"F0.wireOp",EDGE,"E4.68.1")])]});
            var Q121;
            Q121=makeQuery(id+"F1.opExtrude","SWEPT_EDGE",EDGE,{"disambiguationData":[OSD([sQuery(id+"F0.wireOp",EDGE,"E4.67.0"),sQuery(id+"F0.wireOp",EDGE,"E4.67.2")])]});
            var Q122;
            Q122=makeQuery(id+"F1.opExtrude","SWEPT_EDGE",EDGE,{"disambiguationData":[OSD([sQuery(id+"F0.wireOp",EDGE,"E4.67.0"),sQuery(id+"F0.wireOp",EDGE,"E4.67.1")])]});
            var Q123;
            Q123=makeQuery(id+"F1.opExtrude","SWEPT_EDGE",EDGE,{"disambiguationData":[OSD([sQuery(id+"F0.wireOp",EDGE,"E4.66.0"),sQuery(id+"F0.wireOp",EDGE,"E4.66.2")])]});
            var Q124;
            Q124=makeQuery(id+"F1.opExtrude","SWEPT_EDGE",EDGE,{"disambiguationData":[OSD([sQuery(id+"F0.wireOp",EDGE,"E4.66.0"),sQuery(id+"F0.wireOp",EDGE,"E4.66.1")])]});
            var Q125;
            Q125=makeQuery(id+"F1.opExtrude","SWEPT_EDGE",EDGE,{"disambiguationData":[OSD([sQuery(id+"F0.wireOp",EDGE,"E4.65.0"),sQuery(id+"F0.wireOp",EDGE,"E4.65.2")])]});
            var Q126;
            Q126=makeQuery(id+"F1.opExtrude","SWEPT_EDGE",EDGE,{"disambiguationData":[OSD([sQuery(id+"F0.wireOp",EDGE,"E4.65.0"),sQuery(id+"F0.wireOp",EDGE,"E4.65.1")])]});
            var Q127;
            Q127=makeQuery(id+"F1.opExtrude","SWEPT_EDGE",EDGE,{"disambiguationData":[OSD([sQuery(id+"F0.wireOp",EDGE,"E4.64.0"),sQuery(id+"F0.wireOp",EDGE,"E4.64.2")])]});
            var Q128;
            Q128=makeQuery(id+"F1.opExtrude","SWEPT_EDGE",EDGE,{"disambiguationData":[OSD([sQuery(id+"F0.wireOp",EDGE,"E4.64.0"),sQuery(id+"F0.wireOp",EDGE,"E4.64.1")])]});
            var Q129;
            Q129=makeQuery(id+"F1.opExtrude","SWEPT_EDGE",EDGE,{"disambiguationData":[OSD([sQuery(id+"F0.wireOp",EDGE,"E4.63.0"),sQuery(id+"F0.wireOp",EDGE,"E4.63.2")])]});
            var Q130;
            Q130=makeQuery(id+"F1.opExtrude","SWEPT_EDGE",EDGE,{"disambiguationData":[OSD([sQuery(id+"F0.wireOp",EDGE,"E4.63.0"),sQuery(id+"F0.wireOp",EDGE,"E4.63.1")])]});
            var Q131;
            Q131=makeQuery(id+"F1.opExtrude","SWEPT_EDGE",EDGE,{"disambiguationData":[OSD([sQuery(id+"F0.wireOp",EDGE,"E4.62.0"),sQuery(id+"F0.wireOp",EDGE,"E4.62.2")])]});
            var Q132;
            Q132=makeQuery(id+"F1.opExtrude","SWEPT_EDGE",EDGE,{"disambiguationData":[OSD([sQuery(id+"F0.wireOp",EDGE,"E4.62.0"),sQuery(id+"F0.wireOp",EDGE,"E4.62.1")])]});
            var Q133;
            Q133=makeQuery(id+"F1.opExtrude","SWEPT_EDGE",EDGE,{"disambiguationData":[OSD([sQuery(id+"F0.wireOp",EDGE,"E4.61.0"),sQuery(id+"F0.wireOp",EDGE,"E4.61.2")])]});
            var Q134;
            Q134=makeQuery(id+"F1.opExtrude","SWEPT_EDGE",EDGE,{"disambiguationData":[OSD([sQuery(id+"F0.wireOp",EDGE,"E4.61.0"),sQuery(id+"F0.wireOp",EDGE,"E4.61.1")])]});
            var Q135;
            Q135=makeQuery(id+"F1.opExtrude","SWEPT_EDGE",EDGE,{"disambiguationData":[OSD([sQuery(id+"F0.wireOp",EDGE,"E4.59.0"),sQuery(id+"F0.wireOp",EDGE,"E4.59.2")])]});
            var Q136;
            Q136=makeQuery(id+"F1.opExtrude","SWEPT_EDGE",EDGE,{"disambiguationData":[OSD([sQuery(id+"F0.wireOp",EDGE,"E4.59.0"),sQuery(id+"F0.wireOp",EDGE,"E4.59.1")])]});
            var Q137;
            Q137=makeQuery(id+"F1.opExtrude","SWEPT_EDGE",EDGE,{"disambiguationData":[OSD([sQuery(id+"F0.wireOp",EDGE,"E4.60.0"),sQuery(id+"F0.wireOp",EDGE,"E4.60.1")])]});
            var Q138;
            Q138=makeQuery(id+"F1.opExtrude","SWEPT_EDGE",EDGE,{"disambiguationData":[OSD([sQuery(id+"F0.wireOp",EDGE,"E4.60.0"),sQuery(id+"F0.wireOp",EDGE,"E4.60.2")])]});
            var Q139;
            Q139=makeQuery(id+"F1.opExtrude","SWEPT_EDGE",EDGE,{"disambiguationData":[OSD([sQuery(id+"F0.wireOp",EDGE,"E4.76.0"),sQuery(id+"F0.wireOp",EDGE,"E4.76.1")])]});
            var Q140;
            Q140=makeQuery(id+"F1.opExtrude","SWEPT_EDGE",EDGE,{"disambiguationData":[OSD([sQuery(id+"F0.wireOp",EDGE,"E4.58.0"),sQuery(id+"F0.wireOp",EDGE,"E4.58.2")])]});
            var Q141;
            Q141=makeQuery(id+"F1.opExtrude","SWEPT_EDGE",EDGE,{"disambiguationData":[OSD([sQuery(id+"F0.wireOp",EDGE,"E4.58.0"),sQuery(id+"F0.wireOp",EDGE,"E4.58.1")])]});
            var Q142;
            Q142=makeQuery(id+"F1.opExtrude","SWEPT_EDGE",EDGE,{"disambiguationData":[OSD([sQuery(id+"F0.wireOp",EDGE,"E4.57.0"),sQuery(id+"F0.wireOp",EDGE,"E4.57.2")])]});
            var Q143;
            Q143=makeQuery(id+"F1.opExtrude","SWEPT_EDGE",EDGE,{"disambiguationData":[OSD([sQuery(id+"F0.wireOp",EDGE,"E4.57.0"),sQuery(id+"F0.wireOp",EDGE,"E4.57.1")])]});
            var Q144;
            Q144=makeQuery(id+"F1.opExtrude","SWEPT_EDGE",EDGE,{"disambiguationData":[OSD([sQuery(id+"F0.wireOp",EDGE,"E4.56.0"),sQuery(id+"F0.wireOp",EDGE,"E4.56.2")])]});
            var Q145;
            Q145=makeQuery(id+"F1.opExtrude","SWEPT_EDGE",EDGE,{"disambiguationData":[OSD([sQuery(id+"F0.wireOp",EDGE,"E4.56.0"),sQuery(id+"F0.wireOp",EDGE,"E4.56.1")])]});
            var Q146;
            Q146=makeQuery(id+"F1.opExtrude","SWEPT_EDGE",EDGE,{"disambiguationData":[OSD([sQuery(id+"F0.wireOp",EDGE,"E4.55.0"),sQuery(id+"F0.wireOp",EDGE,"E4.55.2")])]});
            var Q147;
            Q147=makeQuery(id+"F1.opExtrude","SWEPT_EDGE",EDGE,{"disambiguationData":[OSD([sQuery(id+"F0.wireOp",EDGE,"E4.55.0"),sQuery(id+"F0.wireOp",EDGE,"E4.55.1")])]});
            var Q148;
            Q148=makeQuery(id+"F1.opExtrude","SWEPT_EDGE",EDGE,{"disambiguationData":[OSD([sQuery(id+"F0.wireOp",EDGE,"E4.54.0"),sQuery(id+"F0.wireOp",EDGE,"E4.54.2")])]});
            var Q149;
            Q149=makeQuery(id+"F1.opExtrude","SWEPT_EDGE",EDGE,{"disambiguationData":[OSD([sQuery(id+"F0.wireOp",EDGE,"E4.54.0"),sQuery(id+"F0.wireOp",EDGE,"E4.54.1")])]});
            var Q150;
            Q150=makeQuery(id+"F1.opExtrude","SWEPT_EDGE",EDGE,{"disambiguationData":[OSD([sQuery(id+"F0.wireOp",EDGE,"E4.53.0"),sQuery(id+"F0.wireOp",EDGE,"E4.53.2")])]});
            var Q151;
            Q151=makeQuery(id+"F1.opExtrude","SWEPT_EDGE",EDGE,{"disambiguationData":[OSD([sQuery(id+"F0.wireOp",EDGE,"E4.53.0"),sQuery(id+"F0.wireOp",EDGE,"E4.53.1")])]});
            var Q152;
            Q152=makeQuery(id+"F1.opExtrude","SWEPT_EDGE",EDGE,{"disambiguationData":[OSD([sQuery(id+"F0.wireOp",EDGE,"E4.52.0"),sQuery(id+"F0.wireOp",EDGE,"E4.52.2")])]});
            var Q153;
            Q153=makeQuery(id+"F1.opExtrude","SWEPT_EDGE",EDGE,{"disambiguationData":[OSD([sQuery(id+"F0.wireOp",EDGE,"E4.52.0"),sQuery(id+"F0.wireOp",EDGE,"E4.52.1")])]});
            fillet(context, id + "F2", {"entities" : qUnion([Q0, Q1, Q2, Q3, Q4, Q5, Q6, Q7, Q8, Q9, Q10, Q11, Q12, Q13, Q14, Q15, Q16, Q17, Q18, Q19, Q20, Q21, Q22, Q23, Q24, Q25, Q26, Q27, Q28, Q29, Q30, Q31, Q32, Q33, Q34, Q35, Q36, Q37, Q38, Q39, Q40, Q41, Q42, Q43, Q44, Q45, Q46, Q47, Q48, Q49, Q50, Q51, Q52, Q53, Q54, Q55, Q56, Q57, Q58, Q59, Q60, Q61, Q62, Q63, Q64, Q65, Q66, Q67, Q68, Q69, Q70, Q71, Q72, Q73, Q74, Q75, Q76, Q77, Q78, Q79, Q80, Q81, Q82, Q83, Q84, Q85, Q86, Q87, Q88, Q89, Q90, Q91, Q92, Q93, Q94, Q95, Q96, Q97, Q98, Q99, Q100, Q101, Q102, Q103, Q104, Q105, Q106, Q107, Q108, Q109, Q110, Q111, Q112, Q113, Q114, Q115, Q116, Q117, Q118, Q119, Q120, Q121, Q122, Q123, Q124, Q125, Q126, Q127, Q128, Q129, Q130, Q131, Q132, Q133, Q134, Q135, Q136, Q137, Q138, Q139, Q140, Q141, Q142, Q143, Q144, Q145, Q146, Q147, Q148, Q149, Q150, Q151, Q152, Q153]), "radius" : 1.5 * mm, "tangentPropagation" : true, "allowEdgeOverflow" : false});
        }
    });
